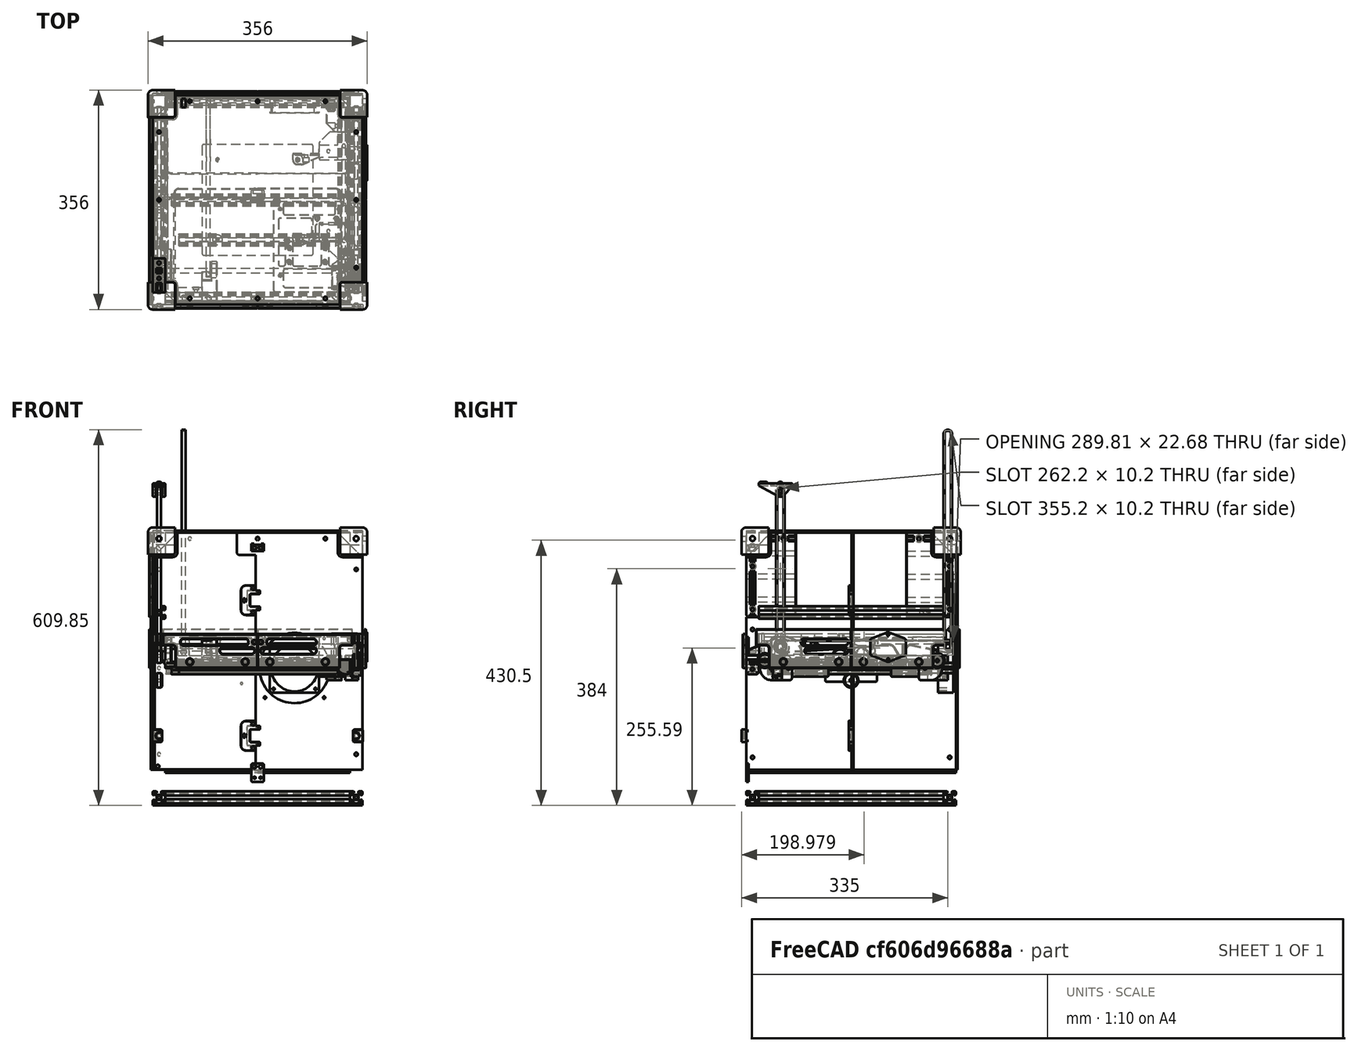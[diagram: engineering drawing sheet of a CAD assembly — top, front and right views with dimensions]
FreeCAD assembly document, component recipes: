
FREECAD ASSEMBLY — COMPONENT RECIPES ("assembly")

This assembly document has 26 components, labeled P0..P25 below (a component is one placed body or linked part). 25 of them carry a construction recipe — the FreeCAD feature program that regenerates the part from scratch, quoted from this document or its linked companion documents; the rest are supplied as boundary geometry only. No exploded tour is included for this assembly.
NOTE — document 2 of 3 of this assembly tour. The two overview renders and the header above are repeated from document 1; the component sections below continue where the previous document stopped.
COMPONENT P13 — recipe-attached ("electronics-mounting-plate", modeled in this document).
Construction recipe (the document's own serialized feature program — sketch geometry with constraints, then the solid features built on it; lengths are millimeters unless a unit is written):

FEATURE [Sketcher::SketchObject] Sketch485
  ArcFitTolerance = 1e-06
  AttachmentSupport = -> [XY_Plane316]
  FullyConstrained = true
  MakeInternals = false
  MapMode = 5
  expr: Constraints[10] = Spreadsheet.side_length / 2 - 20
  expr: Constraints[9] = -Spreadsheet.side_length / 2 + 20
  sketch-geometry (108):
    g0: LineSegment StartX=29 StartY=3 StartZ=0 EndX=147 EndY=3 EndZ=0
    g1: LineSegment StartX=150 StartY=-1e-16 StartZ=0 EndX=150 EndY=-76.5 EndZ=0
    g2: LineSegment StartX=147 StartY=-79.5 StartZ=0 EndX=140.5 EndY=-79.5 EndZ=0
    g3: LineSegment StartX=139.5 StartY=-80.5 StartZ=0 EndX=139.5 EndY=-128 EndZ=0
    g4: LineSegment StartX=138 StartY=-129.5 StartZ=0 EndX=137.5 EndY=-129.5 EndZ=0
    g5: LineSegment StartX=129.5 StartY=-137.5 StartZ=0 EndX=129.5 EndY=-150 EndZ=0
    g6: LineSegment StartX=129.5 StartY=-150 StartZ=0 EndX=29 EndY=-150 EndZ=0
    g7: LineSegment StartX=26 StartY=-147 StartZ=0 EndX=26 EndY=0 EndZ=0
    g8: ArcOfCircle CenterX=29 CenterY=1e-16 CenterZ=0 NormalX=0 NormalY=0 NormalZ=1 AngleXU=0 Radius=3 StartAngle=1.5708 EndAngle=3.14159
    g9: GeomPoint [constr] X=26 Y=3 Z=0
    g10: ArcOfCircle CenterX=147 CenterY=-1e-16 CenterZ=0 NormalX=0 NormalY=0 NormalZ=1 AngleXU=0 Radius=3 StartAngle=0 EndAngle=1.5708
    g11: GeomPoint [constr] X=150 Y=3 Z=0
    g12: ArcOfCircle CenterX=29 CenterY=-147 CenterZ=0 NormalX=0 NormalY=0 NormalZ=1 AngleXU=0 Radius=3 StartAngle=3.14159 EndAngle=4.71239
    g13: GeomPoint [constr] X=26 Y=-150 Z=0
    g14: ArcOfCircle CenterX=137.5 CenterY=-137.5 CenterZ=0 NormalX=0 NormalY=0 NormalZ=1 AngleXU=0 Radius=8 StartAngle=1.5708 EndAngle=3.14159
    g15: GeomPoint [constr] X=129.5 Y=-129.5 Z=0
    g16: ArcOfCircle CenterX=138 CenterY=-128 CenterZ=0 NormalX=0 NormalY=0 NormalZ=1 AngleXU=0 Radius=1.5 StartAngle=4.71239 EndAngle=6.28319
    g17: GeomPoint [constr] X=139.5 Y=-129.5 Z=0
    g18: ArcOfCircle CenterX=147 CenterY=-76.5 CenterZ=0 NormalX=0 NormalY=0 NormalZ=1 AngleXU=0 Radius=3 StartAngle=4.71239 EndAngle=6.28319
    g19: GeomPoint [constr] X=150 Y=-79.5 Z=0
    g20: ArcOfCircle CenterX=140.5 CenterY=-80.5 CenterZ=0 NormalX=0 NormalY=0 NormalZ=1 AngleXU=0 Radius=1 StartAngle=1.5708 EndAngle=3.14159
    g21: GeomPoint [constr] X=139.5 Y=-79.5 Z=0
    g22: LineSegment StartX=42 StartY=-116 StartZ=0 EndX=42 EndY=-139 EndZ=0
    g23: LineSegment StartX=45 StartY=-142 StartZ=0 EndX=118.5 EndY=-142 EndZ=0
    g24: LineSegment StartX=121.5 StartY=-139 StartZ=0 EndX=121.5 EndY=-116 EndZ=0
    g25: LineSegment StartX=118.5 StartY=-113 StartZ=0 EndX=45 EndY=-113 EndZ=0
    g26: LineSegment StartX=34 StartY=-33 StartZ=0 EndX=34 EndY=-58 EndZ=0
    g27: LineSegment StartX=37 StartY=-61 StartZ=0 EndX=85 EndY=-61 EndZ=0
    g28: LineSegment StartX=88 StartY=-58 StartZ=0 EndX=88 EndY=-33 EndZ=0
    g29: LineSegment StartX=85 StartY=-30 StartZ=0 EndX=37 EndY=-30 EndZ=0
    g30: LineSegment StartX=42 StartY=-8 StartZ=0 EndX=42 EndY=-21 EndZ=0
    g31: LineSegment StartX=45 StartY=-24 StartZ=0 EndX=123 EndY=-24 EndZ=0
    g32: LineSegment StartX=126 StartY=-21 StartZ=0 EndX=126 EndY=-8 EndZ=0
    g33: LineSegment StartX=123 StartY=-5 StartZ=0 EndX=45 EndY=-5 EndZ=0
    g34: LineSegment StartX=57 StartY=-70 StartZ=0 EndX=57 EndY=-104 EndZ=0
    g35: LineSegment StartX=60 StartY=-107 StartZ=0 EndX=100.5 EndY=-107 EndZ=0
    g36: LineSegment StartX=103.5 StartY=-104 StartZ=0 EndX=103.5 EndY=-70 EndZ=0
    g37: LineSegment StartX=100.5 StartY=-67 StartZ=0 EndX=60 EndY=-67 EndZ=0
    g38: LineSegment StartX=34 StartY=-76 StartZ=0 EndX=34 EndY=-104 EndZ=0
    g39: LineSegment StartX=37 StartY=-107 StartZ=0 EndX=42 EndY=-107 EndZ=0
    g40: LineSegment StartX=45 StartY=-104 StartZ=0 EndX=45 EndY=-76 EndZ=0
    g41: LineSegment StartX=42 StartY=-73 StartZ=0 EndX=37 EndY=-73 EndZ=0
    g42: LineSegment StartX=115.5 StartY=-70 StartZ=0 EndX=115.5 EndY=-104 EndZ=0
    g43: LineSegment StartX=118.5 StartY=-107 StartZ=0 EndX=128.5 EndY=-107 EndZ=0
    g44: LineSegment StartX=131.5 StartY=-104 StartZ=0 EndX=131.5 EndY=-70 EndZ=0
    g45: LineSegment StartX=128.5 StartY=-67 StartZ=0 EndX=118.5 EndY=-67 EndZ=0
    g46: LineSegment StartX=94 StartY=-43 StartZ=0 EndX=94 EndY=-58 EndZ=0
    g47: LineSegment StartX=97 StartY=-61 StartZ=0 EndX=139 EndY=-61 EndZ=0
    g48: LineSegment StartX=142 StartY=-58 StartZ=0 EndX=142 EndY=-43 EndZ=0
    g49: LineSegment StartX=139 StartY=-40 StartZ=0 EndX=97 EndY=-40 EndZ=0
    g50: GeomPoint X=109.5 Y=-67 Z=0
    g51: GeomPoint X=51 Y=-107 Z=0
    g52: ArcOfCircle CenterX=45 CenterY=-8 CenterZ=0 NormalX=0 NormalY=0 NormalZ=1 AngleXU=0 Radius=3 StartAngle=1.5708 EndAngle=3.14159
    g53: GeomPoint [constr] X=42 Y=-5 Z=0
    g54: ArcOfCircle CenterX=45 CenterY=-21 CenterZ=0 NormalX=0 NormalY=0 NormalZ=1 AngleXU=0 Radius=3 StartAngle=3.14159 EndAngle=4.71239
    g55: GeomPoint [constr] X=42 Y=-24 Z=0
    g56: ArcOfCircle CenterX=123 CenterY=-21 CenterZ=0 NormalX=0 NormalY=0 NormalZ=1 AngleXU=0 Radius=3 StartAngle=4.71239 EndAngle=6.28319
    g57: GeomPoint [constr] X=126 Y=-24 Z=0
    g58: ArcOfCircle CenterX=123 CenterY=-8 CenterZ=0 NormalX=0 NormalY=0 NormalZ=1 AngleXU=0 Radius=3 StartAngle=0 EndAngle=1.5708
    g59: GeomPoint [constr] X=126 Y=-5 Z=0
    g60: ArcOfCircle CenterX=37 CenterY=-33 CenterZ=0 NormalX=0 NormalY=0 NormalZ=1 AngleXU=0 Radius=3 StartAngle=1.5708 EndAngle=3.14159
    g61: GeomPoint [constr] X=34 Y=-30 Z=0
    g62: ArcOfCircle CenterX=85 CenterY=-33 CenterZ=0 NormalX=0 NormalY=0 NormalZ=1 AngleXU=0 Radius=3 StartAngle=2e-16 EndAngle=1.5708
    g63: GeomPoint [constr] X=88 Y=-30 Z=0
    g64: ArcOfCircle CenterX=85 CenterY=-58 CenterZ=0 NormalX=0 NormalY=0 NormalZ=1 AngleXU=0 Radius=3 StartAngle=4.71239 EndAngle=6.28319
    g65: GeomPoint [constr] X=88 Y=-61 Z=0
    g66: ArcOfCircle CenterX=37 CenterY=-58 CenterZ=0 NormalX=0 NormalY=0 NormalZ=1 AngleXU=0 Radius=3 StartAngle=3.14159 EndAngle=4.71239
    g67: GeomPoint [constr] X=34 Y=-61 Z=0
    g68: ArcOfCircle CenterX=97 CenterY=-58 CenterZ=0 NormalX=0 NormalY=0 NormalZ=1 AngleXU=0 Radius=3 StartAngle=3.14159 EndAngle=4.71239
    g69: GeomPoint [constr] X=94 Y=-61 Z=0
    g70: ArcOfCircle CenterX=97 CenterY=-43 CenterZ=0 NormalX=0 NormalY=0 NormalZ=1 AngleXU=0 Radius=3 StartAngle=1.5708 EndAngle=3.14159
    g71: GeomPoint [constr] X=94 Y=-40 Z=0
    g72: ArcOfCircle CenterX=139 CenterY=-43 CenterZ=0 NormalX=0 NormalY=0 NormalZ=1 AngleXU=0 Radius=3 StartAngle=0 EndAngle=1.5708
    g73: GeomPoint [constr] X=142 Y=-40 Z=0
    g74: ArcOfCircle CenterX=139 CenterY=-58 CenterZ=0 NormalX=0 NormalY=0 NormalZ=1 AngleXU=0 Radius=3 StartAngle=4.71239 EndAngle=6.28319
    g75: GeomPoint [constr] X=142 Y=-61 Z=0
    g76: ArcOfCircle CenterX=42 CenterY=-104 CenterZ=0 NormalX=0 NormalY=0 NormalZ=1 AngleXU=0 Radius=3 StartAngle=4.71239 EndAngle=6.28319
    g77: GeomPoint [constr] X=45 Y=-107 Z=0
    g78: ArcOfCircle CenterX=37 CenterY=-104 CenterZ=0 NormalX=0 NormalY=0 NormalZ=1 AngleXU=0 Radius=3 StartAngle=3.14159 EndAngle=4.71239
    g79: GeomPoint [constr] X=34 Y=-107 Z=0
    g80: ArcOfCircle CenterX=37 CenterY=-76 CenterZ=0 NormalX=0 NormalY=0 NormalZ=1 AngleXU=0 Radius=3 StartAngle=1.5708 EndAngle=3.14159
    g81: GeomPoint [constr] X=34 Y=-73 Z=0
    g82: ArcOfCircle CenterX=42 CenterY=-76 CenterZ=0 NormalX=0 NormalY=0 NormalZ=1 AngleXU=0 Radius=3 StartAngle=1.6e-15 EndAngle=1.5708
    g83: GeomPoint [constr] X=45 Y=-73 Z=0
    g84: ArcOfCircle CenterX=60 CenterY=-70 CenterZ=0 NormalX=0 NormalY=0 NormalZ=1 AngleXU=0 Radius=3 StartAngle=1.5708 EndAngle=3.14159
    g85: GeomPoint [constr] X=57 Y=-67 Z=0
    g86: ArcOfCircle CenterX=100.5 CenterY=-70 CenterZ=0 NormalX=0 NormalY=0 NormalZ=1 AngleXU=0 Radius=3 StartAngle=1.6e-15 EndAngle=1.5708
    g87: GeomPoint [constr] X=103.5 Y=-67 Z=0
    g88: ArcOfCircle CenterX=100.5 CenterY=-104 CenterZ=0 NormalX=0 NormalY=0 NormalZ=1 AngleXU=0 Radius=3 StartAngle=4.71239 EndAngle=6.28319
    g89: GeomPoint [constr] X=103.5 Y=-107 Z=0
    g90: ArcOfCircle CenterX=60 CenterY=-104 CenterZ=0 NormalX=0 NormalY=0 NormalZ=1 AngleXU=0 Radius=3 StartAngle=3.14159 EndAngle=4.71239
    g91: GeomPoint [constr] X=57 Y=-107 Z=0
    g92: ArcOfCircle CenterX=118.5 CenterY=-70 CenterZ=0 NormalX=0 NormalY=0 NormalZ=1 AngleXU=0 Radius=3 StartAngle=1.5708 EndAngle=3.14159
    g93: GeomPoint [constr] X=115.5 Y=-67 Z=0
    g94: ArcOfCircle CenterX=128.5 CenterY=-70 CenterZ=0 NormalX=0 NormalY=0 NormalZ=1 AngleXU=0 Radius=3 StartAngle=4e-16 EndAngle=1.5708
    g95: GeomPoint [constr] X=131.5 Y=-67 Z=0
    g96: ArcOfCircle CenterX=128.5 CenterY=-104 CenterZ=0 NormalX=0 NormalY=0 NormalZ=1 AngleXU=0 Radius=3 StartAngle=4.71239 EndAngle=6.28319
    g97: GeomPoint [constr] X=131.5 Y=-107 Z=0
    g98: ArcOfCircle CenterX=118.5 CenterY=-104 CenterZ=0 NormalX=0 NormalY=0 NormalZ=1 AngleXU=0 Radius=3 StartAngle=3.14159 EndAngle=4.71239
    g99: GeomPoint [constr] X=115.5 Y=-107 Z=0
    g100: ArcOfCircle CenterX=45 CenterY=-116 CenterZ=0 NormalX=0 NormalY=0 NormalZ=1 AngleXU=0 Radius=3 StartAngle=1.5708 EndAngle=3.14159
    g101: GeomPoint [constr] X=42 Y=-113 Z=0
    g102: ArcOfCircle CenterX=45 CenterY=-139 CenterZ=0 NormalX=0 NormalY=0 NormalZ=1 AngleXU=0 Radius=3 StartAngle=3.14159 EndAngle=4.71239
    g103: GeomPoint [constr] X=42 Y=-142 Z=0
    g104: ArcOfCircle CenterX=118.5 CenterY=-139 CenterZ=0 NormalX=0 NormalY=0 NormalZ=1 AngleXU=0 Radius=3 StartAngle=4.71239 EndAngle=6.28319
    g105: GeomPoint [constr] X=121.5 Y=-142 Z=0
    g106: ArcOfCircle CenterX=118.5 CenterY=-116 CenterZ=0 NormalX=0 NormalY=0 NormalZ=1 AngleXU=0 Radius=3 StartAngle=1.7e-15 EndAngle=1.5708
    g107: GeomPoint [constr] X=121.5 Y=-113 Z=0
  constraints (250):
    c: Horizontal(g0)
    c: Vertical(g1)
    c: Horizontal(g2)
    c: Vertical(g3)
    c: Horizontal(g4)
    c: Vertical(g5)
    c: Coincident(g5,g6)
    c: Horizontal(g6)
    c: Vertical(g7)
    c: DistanceY(g13) = -150
    c: DistanceX(g11) = 150
    c: DistanceX(g9) = 26
    c: DistanceY(g9) = 3
    c: PointOnObject(g9,g0)
    c: PointOnObject(g9,g7)
    c: Tangent(g0,g8) = 1.5708
    c: Tangent(g7,g8) = 1.5708
    c: Radius(g8) = 3
    c: PointOnObject(g11,g0)
    c: PointOnObject(g11,g1)
    c: Tangent(g0,g10) = 1.5708
    c: Tangent(g1,g10) = 1.5708
    c: PointOnObject(g13,g6)
    c: PointOnObject(g13,g7)
    c: Tangent(g6,g12) = 1.5708
    c: Tangent(g7,g12) = 1.5708
    c: Equal(g12,g10)
    c: Equal(g10,g8)
    c: DistanceX(g21,g19) = 10.5
    c: DistanceY(g5,g19) = 70.5
    c: PointOnObject(g15,g4)
    c: PointOnObject(g15,g5)
    c: Tangent(g4,g14) = -1.5708
    c: Tangent(g5,g14) = -1.5708
    c: Radius(g14) = 8
    c: DistanceX(g5,g19) = 20.5
    c: DistanceY(g5,g17) = 20.5
    c: PointOnObject(g17,g3)
    c: PointOnObject(g17,g4)
    c: Tangent(g3,g16) = 1.5708
    c: Tangent(g4,g16) = 1.5708
    c: PointOnObject(g19,g2)
    c: Tangent(g1,g18) = 1.5708
    c: Tangent(g2,g18) = 1.5708
    c: Equal(g18,g10)
    c: Radius(g16) = 1.5
    c: PointOnObject(g19,g1)
    c: PointOnObject(g21,g2)
    c: PointOnObject(g21,g3)
    c: Tangent(g2,g20) = -1.5708
    c: Tangent(g3,g20) = -1.5708
    c: Radius(g20) = 1
    c: Vertical(g22)
    c: Vertical(g24)
    c: Horizontal(g23)
    c: Horizontal(g25)
    c: Vertical(g26)
    c: Vertical(g28)
    c: Horizontal(g27)
    c: Horizontal(g29)
    c: Vertical(g30)
    c: Vertical(g32)
    c: Horizontal(g31)
    c: Horizontal(g33)
    c: Vertical(g34)
    c: Vertical(g36)
    c: Horizontal(g35)
    c: Horizontal(g37)
    c: Vertical(g38)
    c: Vertical(g40)
    c: Horizontal(g39)
    c: Horizontal(g41)
    c: Vertical(g42)
    c: Vertical(g44)
    c: Horizontal(g43)
    c: Horizontal(g45)
    c: Vertical(g46)
    c: Vertical(g48)
    c: Horizontal(g47)
    c: Horizontal(g49)
    c: Horizontal(g65,g69)
    c: DistanceY(g53,g0) = 8
    c: DistanceY(g61,g55) = 6
    c: DistanceX(g65,g69) = 6
    c: DistanceY(g87,g69) = 6
    c: Horizontal(g93,g87)
    c: Horizontal(g91,g77)
    c: DistanceY(g101,g91) = 6
    c: DistanceX(g87,g93) = 12
    c: DistanceX(g77,g91) = 12
    c: Horizontal(g89,g99)
    c: DistanceX(g105,g5) = 8
    c: DistanceY(g6,g103) = 8
    c: DistanceX(g13,g103) = 16
    c: DistanceY(g83,g67) = 12
    c: DistanceX(g9,g53) = 16
    c: DistanceX(g9,g61) = 8
    c: Vertical(g81,g67)
    c: DistanceX(g59,g11) = 24
    c: DistanceY(g71,g57) = 16
    c: DistanceX(g97,g17) = 8
    c: Symmetric(g93,g87,g50)
    c: DistanceX(g50) = 109.5
    c: DistanceY(g67) = -61
    c: Symmetric(g91,g77,g51)
    c: DistanceX(g51) = 51
    c: DistanceX(g73,g19) = 8
    c: DistanceY(g63) = -30
    c: DistanceY(g77) = -107
    c: DistanceX(g63) = 88
    c: PointOnObject(g53,g30)
    c: PointOnObject(g53,g33)
    c: Tangent(g30,g52) = -1.5708
    c: Tangent(g33,g52) = -1.5708
    c: PointOnObject(g55,g30)
    c: PointOnObject(g55,g31)
    c: Tangent(g30,g54) = -1.5708
    c: Tangent(g31,g54) = -1.5708
    c: PointOnObject(g57,g31)
    c: PointOnObject(g57,g32)
    c: Tangent(g31,g56) = -1.5708
    c: Tangent(g32,g56) = -1.5708
    c: PointOnObject(g59,g32)
    c: PointOnObject(g59,g33)
    c: Tangent(g32,g58) = -1.5708
    c: Tangent(g33,g58) = -1.5708
    c: Equal(g52,g54)
    c: Equal(g54,g56)
    c: Equal(g56,g58)
    c: Radius(g58) = 3
    c: PointOnObject(g61,g26)
    c: PointOnObject(g61,g29)
    c: Tangent(g26,g60) = -1.5708
    c: Tangent(g29,g60) = -1.5708
    c: PointOnObject(g63,g28)
    c: PointOnObject(g63,g29)
    c: Tangent(g28,g62) = -1.5708
    c: Tangent(g29,g62) = -1.5708
    c: PointOnObject(g65,g27)
    c: PointOnObject(g65,g28)
    c: Tangent(g27,g64) = -1.5708
    c: Tangent(g28,g64) = -1.5708
    c: PointOnObject(g67,g26)
    c: PointOnObject(g67,g27)
    c: Tangent(g26,g66) = -1.5708
    c: Tangent(g27,g66) = -1.5708
    c: Equal(g66,g60)
    c: Equal(g60,g62)
    c: Equal(g62,g64)
    c: Equal(g64,g54)
    c: PointOnObject(g69,g46)
    c: PointOnObject(g69,g47)
    c: Tangent(g46,g68) = -1.5708
    c: Tangent(g47,g68) = -1.5708
    c: PointOnObject(g71,g46)
    c: PointOnObject(g71,g49)
    c: Tangent(g46,g70) = -1.5708
    c: Tangent(g49,g70) = -1.5708
    c: PointOnObject(g73,g48)
    c: PointOnObject(g73,g49)
    c: Tangent(g48,g72) = -1.5708
    c: Tangent(g49,g72) = -1.5708
    c: PointOnObject(g75,g47)
    c: PointOnObject(g75,g48)
    c: Tangent(g47,g74) = -1.5708
    c: Tangent(g48,g74) = -1.5708
    c: Equal(g74,g72)
    c: Equal(g72,g70)
    c: Equal(g70,g68)
    c: Equal(g68,g64)
    c: PointOnObject(g77,g39)
    c: PointOnObject(g77,g40)
    c: Tangent(g39,g76) = -1.5708
    c: Tangent(g40,g76) = -1.5708
    c: PointOnObject(g79,g38)
    c: PointOnObject(g79,g39)
    c: Tangent(g38,g78) = -1.5708
    c: Tangent(g39,g78) = -1.5708
    c: PointOnObject(g81,g38)
    c: PointOnObject(g81,g41)
    c: Tangent(g38,g80) = -1.5708
    c: Tangent(g41,g80) = -1.5708
    c: PointOnObject(g83,g40)
    c: PointOnObject(g83,g41)
    c: Tangent(g40,g82) = -1.5708
    c: Tangent(g41,g82) = -1.5708
    c: Equal(g80,g82)
    c: Equal(g82,g76)
    c: Equal(g76,g78)
    c: Equal(g78,g66)
    c: PointOnObject(g85,g34)
    c: PointOnObject(g85,g37)
    c: Tangent(g34,g84) = -1.5708
    c: Tangent(g37,g84) = -1.5708
    c: PointOnObject(g87,g36)
    c: PointOnObject(g87,g37)
    c: Tangent(g36,g86) = -1.5708
    c: Tangent(g37,g86) = -1.5708
    c: PointOnObject(g89,g35)
    c: PointOnObject(g89,g36)
    c: Tangent(g35,g88) = -1.5708
    c: Tangent(g36,g88) = -1.5708
    c: PointOnObject(g91,g34)
    c: PointOnObject(g91,g35)
    c: Tangent(g34,g90) = -1.5708
    c: Tangent(g35,g90) = -1.5708
    c: Equal(g90,g84)
    c: Equal(g84,g86)
    c: Equal(g86,g88)
    c: Equal(g88,g82)
    c: PointOnObject(g93,g42)
    c: PointOnObject(g93,g45)
    c: Tangent(g42,g92) = -1.5708
    c: Tangent(g45,g92) = -1.5708
    c: PointOnObject(g95,g44)
    c: PointOnObject(g95,g45)
    c: Tangent(g44,g94) = -1.5708
    c: Tangent(g45,g94) = -1.5708
    c: PointOnObject(g97,g43)
    c: PointOnObject(g97,g44)
    c: Tangent(g43,g96) = -1.5708
    c: Tangent(g44,g96) = -1.5708
    c: PointOnObject(g99,g42)
    c: PointOnObject(g99,g43)
    c: Tangent(g42,g98) = -1.5708
    c: Tangent(g43,g98) = -1.5708
    c: Equal(g98,g96)
    c: Equal(g96,g94)
    c: Equal(g94,g92)
    c: Equal(g92,g86)
    c: PointOnObject(g101,g22)
    c: PointOnObject(g101,g25)
    c: Tangent(g22,g100) = -1.5708
    c: Tangent(g25,g100) = -1.5708
    c: PointOnObject(g103,g22)
    c: PointOnObject(g103,g23)
    c: Tangent(g22,g102) = -1.5708
    c: Tangent(g23,g102) = -1.5708
    c: PointOnObject(g105,g23)
    c: PointOnObject(g105,g24)
    c: Tangent(g23,g104) = -1.5708
    c: Tangent(g24,g104) = -1.5708
    c: PointOnObject(g107,g24)
    c: PointOnObject(g107,g25)
    c: Tangent(g24,g106) = -1.5708
    c: Tangent(g25,g106) = -1.5708
    c: Equal(g106,g104)
    c: Equal(g104,g100)
    c: Equal(g100,g102)
    c: Equal(g100,g78)
FEATURE [PartDesign::Pad] Pad109
  Direction = (0,0,1)
  Length = 4
  Length2 = 10
  Profile = -> Sketch485
  ReferenceAxis = -> Sketch485 [N_Axis]
  Suppressed = false
  Type = 0
FEATURE [Sketcher::SketchObject] Sketch486
  ArcFitTolerance = 1e-06
  AttachmentOffset = pos=(0,0,4) rot=(0,0,1;0rad)
  AttachmentSupport = -> [XY_Plane316]
  FullyConstrained = true
  MakeInternals = false
  MapMode = 5
  Placement = pos=(0,0,4) rot=(0,0,1;0rad)
  sketch-geometry (10):
    g0: Circle CenterX=32 CenterY=-2.5 CenterZ=0 NormalX=0 NormalY=0 NormalZ=1 AngleXU=0 Radius=3
    g1: Circle CenterX=96 CenterY=-29.5 CenterZ=0 NormalX=0 NormalY=0 NormalZ=1 AngleXU=0 Radius=3
    g2: Circle CenterX=128 CenterY=-32 CenterZ=0 NormalX=0 NormalY=0 NormalZ=1 AngleXU=0 Radius=3
    g3: Circle CenterX=47.5 CenterY=-67 CenterZ=0 NormalX=0 NormalY=0 NormalZ=1 AngleXU=0 Radius=3
    g4: Circle CenterX=109.5 CenterY=-67 CenterZ=0 NormalX=0 NormalY=0 NormalZ=1 AngleXU=0 Radius=3
    g5: Circle CenterX=51 CenterY=-78.5 CenterZ=0 NormalX=0 NormalY=0 NormalZ=1 AngleXU=0 Radius=2.5
    g6: Circle CenterX=109 CenterY=-78.5 CenterZ=0 NormalX=0 NormalY=0 NormalZ=1 AngleXU=0 Radius=2.5
    g7: Circle CenterX=109 CenterY=-101.5 CenterZ=0 NormalX=0 NormalY=0 NormalZ=1 AngleXU=0 Radius=2.5
    g8: Circle CenterX=51 CenterY=-101.5 CenterZ=0 NormalX=0 NormalY=0 NormalZ=1 AngleXU=0 Radius=2.5
    g9: GeomPoint X=80 Y=-90 Z=0
  constraints (28):
    c: Equal(g0,g3)
    c: Equal(g3,g1)
    c: Equal(g1,g4)
    c: Equal(g4,g2)
    c: Diameter(g0) = 6
    c: DistanceX(g0) = 32
    c: DistanceY(g0) = -2.5
    c: Horizontal(g3,g4)
    c: DistanceY(g3) = -67
    c: DistanceX(g3) = 47.5
    c: DistanceX(g4) = 109.5
    c: DistanceX(g1) = 96
    c: DistanceY(g2,g1) = 2.5
    c: DistanceY(g1) = -29.5
    c: DistanceX(g2) = 128
    c: Equal(g5,g6)
    c: Equal(g6,g7)
    c: Equal(g7,g8)
    c: Diameter(g8) = 5
    c: Vertical(g8,g5)
    c: Vertical(g6,g7)
    c: Horizontal(g6,g5)
    c: Horizontal(g8,g7)
    c: Symmetric(g6,g8,g9)
    c: DistanceX(g9) = 80
    c: DistanceY(g9) = -90
    c: DistanceY(g8,g5) = 23
    c: DistanceX(g5,g6) = 58
FEATURE [PartDesign::Pad] Pad110
  BaseFeature = -> Pad109
  Direction = (0,0,1)
  Length = 3
  Length2 = 10
  Profile = -> Sketch486
  ReferenceAxis = -> Sketch486 [N_Axis]
  Suppressed = false
  Type = 0
FEATURE [Sketcher::SketchObject] Sketch487
  ArcFitTolerance = 1e-06
  AttachmentOffset = pos=(0,0,4.3) rot=(0,0,1;0rad)
  AttachmentSupport = -> [XY_Plane316]
  FullyConstrained = true
  MakeInternals = false
  MapMode = 5
  Placement = pos=(0,0,4.3) rot=(0,0,1;0rad)
  sketch-geometry (10):
    g0: Circle CenterX=32 CenterY=-2.5 CenterZ=0 NormalX=0 NormalY=0 NormalZ=1 AngleXU=0 Radius=1.75
    g1: Circle CenterX=96 CenterY=-29.5 CenterZ=0 NormalX=0 NormalY=0 NormalZ=1 AngleXU=0 Radius=1.75
    g2: Circle CenterX=128 CenterY=-32 CenterZ=0 NormalX=0 NormalY=0 NormalZ=1 AngleXU=0 Radius=1.75
    g3: Circle CenterX=47.5 CenterY=-67 CenterZ=0 NormalX=0 NormalY=0 NormalZ=1 AngleXU=0 Radius=1.75
    g4: Circle CenterX=109.5 CenterY=-67 CenterZ=0 NormalX=0 NormalY=0 NormalZ=1 AngleXU=0 Radius=1.75
    g5: Circle CenterX=51 CenterY=-78.5 CenterZ=0 NormalX=0 NormalY=0 NormalZ=1 AngleXU=0 Radius=1.5
    g6: Circle CenterX=109 CenterY=-78.5 CenterZ=0 NormalX=0 NormalY=0 NormalZ=1 AngleXU=0 Radius=1.5
    g7: Circle CenterX=109 CenterY=-101.5 CenterZ=0 NormalX=0 NormalY=0 NormalZ=1 AngleXU=0 Radius=1.5
    g8: Circle CenterX=51 CenterY=-101.5 CenterZ=0 NormalX=0 NormalY=0 NormalZ=1 AngleXU=0 Radius=1.5
    g9: GeomPoint X=80 Y=-90 Z=0
  constraints (28):
    c: Equal(g0,g3)
    c: Equal(g3,g1)
    c: Equal(g1,g4)
    c: Equal(g4,g2)
    c: Diameter(g0) = 3.5
    c: DistanceX(g0) = 32
    c: DistanceY(g0) = -2.5
    c: Horizontal(g3,g4)
    c: DistanceY(g3) = -67
    c: DistanceX(g3) = 47.5
    c: DistanceX(g4) = 109.5
    c: DistanceX(g1) = 96
    c: DistanceY(g2,g1) = 2.5
    c: DistanceY(g1) = -29.5
    c: DistanceX(g2) = 128
    c: Equal(g5,g6)
    c: Equal(g6,g7)
    c: Equal(g7,g8)
    c: Diameter(g8) = 3
    c: Vertical(g8,g5)
    c: Vertical(g6,g7)
    c: Horizontal(g6,g5)
    c: Horizontal(g8,g7)
    c: Symmetric(g6,g8,g9)
    c: DistanceX(g9) = 80
    c: DistanceY(g9) = -90
    c: DistanceY(g8,g5) = 23
    c: DistanceX(g5,g6) = 58
FEATURE [Sketcher::SketchObject] Sketch488
  ArcFitTolerance = 1e-06
  AttachmentOffset = pos=(0,0,4) rot=(0,0,1;0rad)
  AttachmentSupport = -> [XY_Plane316]
  FullyConstrained = true
  MakeInternals = false
  MapMode = 5
  Placement = pos=(0,0,4) rot=(0,0,1;0rad)
  sketch-geometry (73):
    g0: Circle [constr] CenterX=32 CenterY=-2.5 CenterZ=0 NormalX=0 NormalY=0 NormalZ=1 AngleXU=0 Radius=3.17543
    g1: Circle [constr] CenterX=96 CenterY=-29.5 CenterZ=0 NormalX=0 NormalY=0 NormalZ=1 AngleXU=0 Radius=3.17543
    g2: Circle [constr] CenterX=128 CenterY=-32 CenterZ=0 NormalX=0 NormalY=0 NormalZ=1 AngleXU=0 Radius=3.17543
    g3: Circle [constr] CenterX=47.5 CenterY=-67 CenterZ=0 NormalX=0 NormalY=0 NormalZ=1 AngleXU=0 Radius=3.17543
    g4: Circle [constr] CenterX=109.5 CenterY=-67 CenterZ=0 NormalX=0 NormalY=0 NormalZ=1 AngleXU=0 Radius=3.17543
    g5: Circle [constr] CenterX=51 CenterY=-78.5 CenterZ=0 NormalX=0 NormalY=0 NormalZ=1 AngleXU=0 Radius=2.82902
    g6: Circle [constr] CenterX=109 CenterY=-78.5 CenterZ=0 NormalX=0 NormalY=0 NormalZ=1 AngleXU=0 Radius=2.82902
    g7: Circle [constr] CenterX=109 CenterY=-101.5 CenterZ=0 NormalX=0 NormalY=0 NormalZ=1 AngleXU=0 Radius=2.82902
    g8: Circle [constr] CenterX=51 CenterY=-101.5 CenterZ=0 NormalX=0 NormalY=0 NormalZ=1 AngleXU=0 Radius=2.82902
    g9: GeomPoint X=80 Y=-90 Z=0
    g10: LineSegment StartX=35.1754 StartY=-2.5 StartZ=0 EndX=33.5877 EndY=0.25 EndZ=0
    g11: LineSegment StartX=33.5877 StartY=0.25 StartZ=0 EndX=30.4123 EndY=0.25 EndZ=0
    g12: LineSegment StartX=30.4123 StartY=0.25 StartZ=0 EndX=28.8246 EndY=-2.5 EndZ=0
    g13: LineSegment StartX=28.8246 StartY=-2.5 StartZ=0 EndX=30.4123 EndY=-5.25 EndZ=0
    g14: LineSegment StartX=30.4123 StartY=-5.25 StartZ=0 EndX=33.5877 EndY=-5.25 EndZ=0
    g15: LineSegment StartX=33.5877 StartY=-5.25 StartZ=0 EndX=35.1754 EndY=-2.5 EndZ=0
    g16: Circle [constr] CenterX=32 CenterY=-2.5 CenterZ=0 NormalX=0 NormalY=0 NormalZ=1 AngleXU=0 Radius=3.17543
    g17: LineSegment StartX=99.1754 StartY=-29.5 StartZ=0 EndX=97.5877 EndY=-26.75 EndZ=0
    g18: LineSegment StartX=97.5877 StartY=-26.75 StartZ=0 EndX=94.4123 EndY=-26.75 EndZ=0
    g19: LineSegment StartX=94.4123 StartY=-26.75 StartZ=0 EndX=92.8246 EndY=-29.5 EndZ=0
    g20: LineSegment StartX=92.8246 StartY=-29.5 StartZ=0 EndX=94.4123 EndY=-32.25 EndZ=0
    g21: LineSegment StartX=94.4123 StartY=-32.25 StartZ=0 EndX=97.5877 EndY=-32.25 EndZ=0
    g22: LineSegment StartX=97.5877 StartY=-32.25 StartZ=0 EndX=99.1754 EndY=-29.5 EndZ=0
    g23: Circle [constr] CenterX=96 CenterY=-29.5 CenterZ=0 NormalX=0 NormalY=0 NormalZ=1 AngleXU=0 Radius=3.17543
    g24: LineSegment StartX=131.175 StartY=-32 StartZ=0 EndX=129.588 EndY=-29.25 EndZ=0
    g25: LineSegment StartX=129.588 StartY=-29.25 StartZ=0 EndX=126.412 EndY=-29.25 EndZ=0
    g26: LineSegment StartX=126.412 StartY=-29.25 StartZ=0 EndX=124.825 EndY=-32 EndZ=0
    g27: LineSegment StartX=124.825 StartY=-32 StartZ=0 EndX=126.412 EndY=-34.75 EndZ=0
    g28: LineSegment StartX=126.412 StartY=-34.75 StartZ=0 EndX=129.588 EndY=-34.75 EndZ=0
    g29: LineSegment StartX=129.588 StartY=-34.75 StartZ=0 EndX=131.175 EndY=-32 EndZ=0
    g30: Circle [constr] CenterX=128 CenterY=-32 CenterZ=0 NormalX=0 NormalY=0 NormalZ=1 AngleXU=0 Radius=3.17543
    g31: LineSegment StartX=50.6754 StartY=-67 StartZ=0 EndX=49.0877 EndY=-64.25 EndZ=0
    g32: LineSegment StartX=49.0877 StartY=-64.25 StartZ=0 EndX=45.9123 EndY=-64.25 EndZ=0
    g33: LineSegment StartX=45.9123 StartY=-64.25 StartZ=0 EndX=44.3246 EndY=-67 EndZ=0
    g34: LineSegment StartX=44.3246 StartY=-67 StartZ=0 EndX=45.9123 EndY=-69.75 EndZ=0
    g35: LineSegment StartX=45.9123 StartY=-69.75 StartZ=0 EndX=49.0877 EndY=-69.75 EndZ=0
    g36: LineSegment StartX=49.0877 StartY=-69.75 StartZ=0 EndX=50.6754 EndY=-67 EndZ=0
    g37: Circle [constr] CenterX=47.5 CenterY=-67 CenterZ=0 NormalX=0 NormalY=0 NormalZ=1 AngleXU=0 Radius=3.17543
    g38: LineSegment StartX=112.675 StartY=-67 StartZ=0 EndX=111.088 EndY=-64.25 EndZ=0
    g39: LineSegment StartX=111.088 StartY=-64.25 StartZ=0 EndX=107.912 EndY=-64.25 EndZ=0
    g40: LineSegment StartX=107.912 StartY=-64.25 StartZ=0 EndX=106.325 EndY=-67 EndZ=0
    g41: LineSegment StartX=106.325 StartY=-67 StartZ=0 EndX=107.912 EndY=-69.75 EndZ=0
    g42: LineSegment StartX=107.912 StartY=-69.75 StartZ=0 EndX=111.088 EndY=-69.75 EndZ=0
    g43: LineSegment StartX=111.088 StartY=-69.75 StartZ=0 EndX=112.675 EndY=-67 EndZ=0
    g44: Circle [constr] CenterX=109.5 CenterY=-67 CenterZ=0 NormalX=0 NormalY=0 NormalZ=1 AngleXU=0 Radius=3.17543
    g45: LineSegment StartX=53.829 StartY=-78.5 StartZ=0 EndX=52.4145 EndY=-76.05 EndZ=0
    g46: LineSegment StartX=52.4145 StartY=-76.05 StartZ=0 EndX=49.5855 EndY=-76.05 EndZ=0
    g47: LineSegment StartX=49.5855 StartY=-76.05 StartZ=0 EndX=48.171 EndY=-78.5 EndZ=0
    g48: LineSegment StartX=48.171 StartY=-78.5 StartZ=0 EndX=49.5855 EndY=-80.95 EndZ=0
    g49: LineSegment StartX=49.5855 StartY=-80.95 StartZ=0 EndX=52.4145 EndY=-80.95 EndZ=0
    g50: LineSegment StartX=52.4145 StartY=-80.95 StartZ=0 EndX=53.829 EndY=-78.5 EndZ=0
    g51: Circle [constr] CenterX=51 CenterY=-78.5 CenterZ=0 NormalX=0 NormalY=0 NormalZ=1 AngleXU=0 Radius=2.82902
    g52: LineSegment StartX=111.829 StartY=-78.5 StartZ=0 EndX=110.415 EndY=-76.05 EndZ=0
    g53: LineSegment StartX=110.415 StartY=-76.05 StartZ=0 EndX=107.585 EndY=-76.05 EndZ=0
    g54: LineSegment StartX=107.585 StartY=-76.05 StartZ=0 EndX=106.171 EndY=-78.5 EndZ=0
    g55: LineSegment StartX=106.171 StartY=-78.5 StartZ=0 EndX=107.585 EndY=-80.95 EndZ=0
    g56: LineSegment StartX=107.585 StartY=-80.95 StartZ=0 EndX=110.415 EndY=-80.95 EndZ=0
    g57: LineSegment StartX=110.415 StartY=-80.95 StartZ=0 EndX=111.829 EndY=-78.5 EndZ=0
    g58: Circle [constr] CenterX=109 CenterY=-78.5 CenterZ=0 NormalX=0 NormalY=0 NormalZ=1 AngleXU=0 Radius=2.82902
    g59: LineSegment StartX=111.829 StartY=-101.5 StartZ=0 EndX=110.415 EndY=-99.05 EndZ=0
    g60: LineSegment StartX=110.415 StartY=-99.05 StartZ=0 EndX=107.585 EndY=-99.05 EndZ=0
    g61: LineSegment StartX=107.585 StartY=-99.05 StartZ=0 EndX=106.171 EndY=-101.5 EndZ=0
    g62: LineSegment StartX=106.171 StartY=-101.5 StartZ=0 EndX=107.585 EndY=-103.95 EndZ=0
    g63: LineSegment StartX=107.585 StartY=-103.95 StartZ=0 EndX=110.415 EndY=-103.95 EndZ=0
    g64: LineSegment StartX=110.415 StartY=-103.95 StartZ=0 EndX=111.829 EndY=-101.5 EndZ=0
    g65: Circle [constr] CenterX=109 CenterY=-101.5 CenterZ=0 NormalX=0 NormalY=0 NormalZ=1 AngleXU=0 Radius=2.82902
    g66: LineSegment StartX=53.829 StartY=-101.5 StartZ=0 EndX=52.4145 EndY=-99.05 EndZ=0
    g67: LineSegment StartX=52.4145 StartY=-99.05 StartZ=0 EndX=49.5855 EndY=-99.05 EndZ=0
    g68: LineSegment StartX=49.5855 StartY=-99.05 StartZ=0 EndX=48.171 EndY=-101.5 EndZ=0
    g69: LineSegment StartX=48.171 StartY=-101.5 StartZ=0 EndX=49.5855 EndY=-103.95 EndZ=0
    g70: LineSegment StartX=49.5855 StartY=-103.95 StartZ=0 EndX=52.4145 EndY=-103.95 EndZ=0
    g71: LineSegment StartX=52.4145 StartY=-103.95 StartZ=0 EndX=53.829 EndY=-101.5 EndZ=0
    g72: Circle [constr] CenterX=51 CenterY=-101.5 CenterZ=0 NormalX=0 NormalY=0 NormalZ=1 AngleXU=0 Radius=2.82902
  constraints (172):
    c: Equal(g0,g3)
    c: Equal(g3,g1)
    c: Equal(g1,g4)
    c: Equal(g4,g2)
    c: DistanceX(g0) = 32
    c: DistanceY(g0) = -2.5
    c: Horizontal(g3,g4)
    c: DistanceY(g3) = -67
    c: DistanceX(g3) = 47.5
    c: DistanceX(g4) = 109.5
    c: DistanceX(g1) = 96
    c: DistanceY(g2,g1) = 2.5
    c: DistanceY(g1) = -29.5
    c: DistanceX(g2) = 128
    c: Equal(g5,g6)
    c: Equal(g6,g7)
    c: Equal(g7,g8)
    c: Vertical(g8,g5)
    c: Vertical(g6,g7)
    c: Horizontal(g6,g5)
    c: Horizontal(g8,g7)
    c: Symmetric(g6,g8,g9)
    c: DistanceX(g9) = 80
    c: DistanceY(g9) = -90
    c: DistanceY(g8,g5) = 23
    c: DistanceX(g5,g6) = 58
    c: Coincident(g10,g11)
    c: Coincident(g11,g12)
    c: Coincident(g12,g13)
    c: Coincident(g13,g14)
    c: Coincident(g14,g15)
    c: Coincident(g15,g10)
    c: Equal(g10, g11-g15) x5
    c: PointOnObject(g10,g16)
    c: PointOnObject(g11,g16)
    c: PointOnObject(g12,g16)
    c: PointOnObject(g13,g16)
    c: PointOnObject(g14,g16)
    c: PointOnObject(g15,g16)
    c: Coincident(g16,g0)
    c: PointOnObject(g15,g0)
    c: Horizontal(g11)
    c: DistanceY(g14,g10) = 5.5
    c: Coincident(g17,g18)
    c: Coincident(g18,g19)
    c: Coincident(g19,g20)
    c: Coincident(g20,g21)
    c: Coincident(g21,g22)
    c: Coincident(g22,g17)
    c: Equal(g17, g18-g22) x5
    c: PointOnObject(g17,g23)
    c: PointOnObject(g18,g23)
    c: PointOnObject(g19,g23)
    c: PointOnObject(g20,g23)
    c: PointOnObject(g21,g23)
    c: PointOnObject(g22,g23)
    c: Coincident(g23,g1)
    c: PointOnObject(g22,g1)
    c: Horizontal(g18)
    c: Coincident(g24,g25)
    c: Coincident(g25,g26)
    c: Coincident(g26,g27)
    c: Coincident(g27,g28)
    c: Coincident(g28,g29)
    c: Coincident(g29,g24)
    c: Equal(g24, g25-g29) x5
    c: PointOnObject(g24,g30)
    c: PointOnObject(g25,g30)
    c: PointOnObject(g26,g30)
    c: PointOnObject(g27,g30)
    c: PointOnObject(g28,g30)
    c: PointOnObject(g29,g30)
    c: Coincident(g30,g2)
    c: PointOnObject(g29,g2)
    c: Horizontal(g25)
    c: Coincident(g31,g32)
    c: Coincident(g32,g33)
    c: Coincident(g33,g34)
    c: Coincident(g34,g35)
    c: Coincident(g35,g36)
    c: Coincident(g36,g31)
    c: Equal(g31, g32-g36) x5
    c: PointOnObject(g31,g37)
    c: PointOnObject(g32,g37)
    c: PointOnObject(g33,g37)
    c: PointOnObject(g34,g37)
    c: PointOnObject(g35,g37)
    c: PointOnObject(g36,g37)
    c: Coincident(g37,g3)
    c: PointOnObject(g36,g3)
    c: Horizontal(g32)
    c: Coincident(g38,g39)
    c: Coincident(g39,g40)
    c: Coincident(g40,g41)
    c: Coincident(g41,g42)
    c: Coincident(g42,g43)
    c: Coincident(g43,g38)
    c: Equal(g38, g39-g43) x5
    c: PointOnObject(g38,g44)
    c: PointOnObject(g39,g44)
    c: PointOnObject(g40,g44)
    c: PointOnObject(g41,g44)
    c: PointOnObject(g42,g44)
    c: PointOnObject(g43,g44)
    c: Coincident(g44,g4)
    c: PointOnObject(g43,g4)
    c: Horizontal(g39)
    c: Coincident(g45,g46)
    c: Coincident(g46,g47)
    c: Coincident(g47,g48)
    c: Coincident(g48,g49)
    c: Coincident(g49,g50)
    c: Coincident(g50,g45)
    c: Equal(g45, g46-g50) x5
    c: PointOnObject(g45,g51)
    c: PointOnObject(g46,g51)
    c: PointOnObject(g47,g51)
    c: PointOnObject(g48,g51)
    c: PointOnObject(g49,g51)
    c: PointOnObject(g50,g51)
    c: Coincident(g51,g5)
    c: PointOnObject(g50,g5)
    c: Horizontal(g46)
    c: Coincident(g52,g53)
    c: Coincident(g53,g54)
    c: Coincident(g54,g55)
    c: Coincident(g55,g56)
    c: Coincident(g56,g57)
    c: Coincident(g57,g52)
    c: Equal(g52, g53-g57) x5
    c: PointOnObject(g52,g58)
    c: PointOnObject(g53,g58)
    c: PointOnObject(g54,g58)
    c: PointOnObject(g55,g58)
    c: PointOnObject(g56,g58)
    c: PointOnObject(g57,g58)
    c: Coincident(g58,g6)
    c: PointOnObject(g57,g6)
    c: Coincident(g59,g60)
    c: Coincident(g60,g61)
    c: Coincident(g61,g62)
    c: Coincident(g62,g63)
    c: Coincident(g63,g64)
    c: Coincident(g64,g59)
    c: Equal(g59, g60-g64) x5
    c: PointOnObject(g59,g65)
    c: PointOnObject(g60,g65)
    c: PointOnObject(g61,g65)
    c: PointOnObject(g62,g65)
    c: PointOnObject(g63,g65)
    c: PointOnObject(g64,g65)
    c: Coincident(g65,g7)
    c: PointOnObject(g64,g7)
    c: Coincident(g66,g67)
    c: Coincident(g67,g68)
    c: Coincident(g68,g69)
    c: Coincident(g69,g70)
    c: Coincident(g70,g71)
    c: Coincident(g71,g66)
    c: Equal(g66, g67-g71) x5
    c: PointOnObject(g66,g72)
    c: PointOnObject(g67,g72)
    c: PointOnObject(g68,g72)
    c: PointOnObject(g69,g72)
    c: PointOnObject(g70,g72)
    c: PointOnObject(g71,g72)
    c: Coincident(g72,g8)
    c: PointOnObject(g71,g8)
    c: Horizontal(g67)
    c: Horizontal(g60)
    c: Horizontal(g53)
    c: DistanceY(g70,g66) = 4.9
FEATURE [PartDesign::Chamfer] Chamfer021
  Angle = 45
  Base = -> Pad110 [Edge136,Edge127,Edge145,Edge154,Edge155,Edge108,Edge107,Edge118,Edge117]
  BaseFeature = -> Pad110
  ChamferType = 0
  FlipDirection = false
  Size = 2
  Size2 = 1
  SupportTransform = false
  Suppressed = false
  UseAllEdges = false
FEATURE [PartDesign::Pocket] Pocket341
  BaseFeature = -> Chamfer021
  Direction = (0,0,-1)
  Length = 5
  Length2 = 5
  Profile = -> Sketch487
  ReferenceAxis = -> Sketch487 [N_Axis]
  Reversed = true
  Suppressed = false
  Type = 1
FEATURE [PartDesign::Pocket] Pocket342
  BaseFeature = -> Pocket341
  Direction = (0,0,-1)
  Length = 5
  Length2 = 5
  Profile = -> Sketch488
  ReferenceAxis = -> Sketch488 [N_Axis]
  Suppressed = false
  Type = 1
FEATURE [Sketcher::SketchObject] Sketch489
  ArcFitTolerance = 1e-06
  AttachmentOffset = pos=(0,0,0.7) rot=(0,0,1;0rad)
  AttachmentSupport = -> [XY_Plane316]
  FullyConstrained = true
  MakeInternals = false
  MapMode = 5
  Placement = pos=(0,0,0.7) rot=(0,0,1;0rad)
  sketch-geometry (4):
    g0: Circle CenterX=37 CenterY=-15 CenterZ=0 NormalX=0 NormalY=0 NormalZ=1 AngleXU=0 Radius=1.75
    g1: Circle CenterX=132 CenterY=-15 CenterZ=0 NormalX=0 NormalY=0 NormalZ=1 AngleXU=0 Radius=1.75
    g2: Circle CenterX=37 CenterY=-123 CenterZ=0 NormalX=0 NormalY=0 NormalZ=1 AngleXU=0 Radius=1.75
    g3: Circle CenterX=132 CenterY=-123 CenterZ=0 NormalX=0 NormalY=0 NormalZ=1 AngleXU=0 Radius=1.75
  constraints (12):
    c: Horizontal(g2,g3)
    c: Equal(g2,g3)
    c: Diameter(g2) = 3.5
    c: Equal(g0,g1)
    c: Equal(g1,g3)
    c: Horizontal(g0,g1)
    c: Vertical(g1,g3)
    c: Vertical(g0,g2)
    c: DistanceX(g0) = 37
    c: DistanceY(g0) = -15
    c: DistanceX(g1) = 132
    c: DistanceY(g2) = -123
FEATURE [PartDesign::Pocket] Pocket343
  BaseFeature = -> Pocket342
  Direction = (0,0,-1)
  Length = 5
  Length2 = 5
  Midplane = true
  Profile = -> Sketch489
  ReferenceAxis = -> Sketch489 [N_Axis]
  Suppressed = false
  Type = 1
FEATURE [Sketcher::SketchObject] Sketch490
  ArcFitTolerance = 1e-06
  AttachmentOffset = pos=(0,0,1) rot=(0,0,1;0rad)
  AttachmentSupport = -> [XY_Plane316]
  FullyConstrained = true
  MakeInternals = false
  MapMode = 5
  Placement = pos=(0,0,1) rot=(0,0,1;0rad)
  sketch-geometry (28):
    g0: LineSegment StartX=38.5877 StartY=-17.75 StartZ=0 EndX=40.1754 EndY=-15 EndZ=0
    g1: LineSegment StartX=40.1754 StartY=-15 StartZ=0 EndX=38.5877 EndY=-12.25 EndZ=0
    g2: LineSegment StartX=38.5877 StartY=-12.25 StartZ=0 EndX=35.4123 EndY=-12.25 EndZ=0
    g3: LineSegment StartX=35.4123 StartY=-12.25 StartZ=0 EndX=33.8246 EndY=-15 EndZ=0
    g4: LineSegment StartX=33.8246 StartY=-15 StartZ=0 EndX=35.4123 EndY=-17.75 EndZ=0
    g5: LineSegment StartX=35.4123 StartY=-17.75 StartZ=0 EndX=38.5877 EndY=-17.75 EndZ=0
    g6: Circle [constr] CenterX=37 CenterY=-15 CenterZ=0 NormalX=0 NormalY=0 NormalZ=1 AngleXU=0 Radius=3.17543
    g7: LineSegment StartX=133.588 StartY=-17.75 StartZ=0 EndX=135.175 EndY=-15 EndZ=0
    g8: LineSegment StartX=135.175 StartY=-15 StartZ=0 EndX=133.588 EndY=-12.25 EndZ=0
    g9: LineSegment StartX=133.588 StartY=-12.25 StartZ=0 EndX=130.412 EndY=-12.25 EndZ=0
    g10: LineSegment StartX=130.412 StartY=-12.25 StartZ=0 EndX=128.825 EndY=-15 EndZ=0
    g11: LineSegment StartX=128.825 StartY=-15 StartZ=0 EndX=130.412 EndY=-17.75 EndZ=0
    g12: LineSegment StartX=130.412 StartY=-17.75 StartZ=0 EndX=133.588 EndY=-17.75 EndZ=0
    g13: Circle [constr] CenterX=132 CenterY=-15 CenterZ=0 NormalX=0 NormalY=0 NormalZ=1 AngleXU=0 Radius=3.17543
    g14: LineSegment StartX=133.588 StartY=-125.75 StartZ=0 EndX=135.175 EndY=-123 EndZ=0
    g15: LineSegment StartX=135.175 StartY=-123 StartZ=0 EndX=133.588 EndY=-120.25 EndZ=0
    g16: LineSegment StartX=133.588 StartY=-120.25 StartZ=0 EndX=130.412 EndY=-120.25 EndZ=0
    g17: LineSegment StartX=130.412 StartY=-120.25 StartZ=0 EndX=128.825 EndY=-123 EndZ=0
    g18: LineSegment StartX=128.825 StartY=-123 StartZ=0 EndX=130.412 EndY=-125.75 EndZ=0
    g19: LineSegment StartX=130.412 StartY=-125.75 StartZ=0 EndX=133.588 EndY=-125.75 EndZ=0
    g20: Circle [constr] CenterX=132 CenterY=-123 CenterZ=0 NormalX=0 NormalY=0 NormalZ=1 AngleXU=0 Radius=3.17543
    g21: LineSegment StartX=40.1754 StartY=-123 StartZ=0 EndX=38.5877 EndY=-120.25 EndZ=0
    g22: LineSegment StartX=38.5877 StartY=-120.25 StartZ=0 EndX=35.4123 EndY=-120.25 EndZ=0
    g23: LineSegment StartX=35.4123 StartY=-120.25 StartZ=0 EndX=33.8246 EndY=-123 EndZ=0
    g24: LineSegment StartX=33.8246 StartY=-123 StartZ=0 EndX=35.4123 EndY=-125.75 EndZ=0
    g25: LineSegment StartX=35.4123 StartY=-125.75 StartZ=0 EndX=38.5877 EndY=-125.75 EndZ=0
    g26: LineSegment StartX=38.5877 StartY=-125.75 StartZ=0 EndX=40.1754 EndY=-123 EndZ=0
    g27: Circle [constr] CenterX=37 CenterY=-123 CenterZ=0 NormalX=0 NormalY=0 NormalZ=1 AngleXU=0 Radius=3.17543
  constraints (68):
    c: Coincident(g0,g1)
    c: Coincident(g1,g2)
    c: Coincident(g2,g3)
    c: Coincident(g3,g4)
    c: Coincident(g4,g5)
    c: Coincident(g5,g0)
    c: Equal(g0, g1-g5) x5
    c: PointOnObject(g0,g6)
    c: PointOnObject(g1,g6)
    c: PointOnObject(g2,g6)
    c: PointOnObject(g3,g6)
    c: PointOnObject(g4,g6)
    c: PointOnObject(g5,g6)
    c: Coincident(g7,g8)
    c: Coincident(g8,g9)
    c: Coincident(g9,g10)
    c: Coincident(g10,g11)
    c: Coincident(g11,g12)
    c: Coincident(g12,g7)
    c: Equal(g7, g8-g12) x5
    c: PointOnObject(g7,g13)
    c: PointOnObject(g8,g13)
    c: PointOnObject(g9,g13)
    c: PointOnObject(g10,g13)
    c: PointOnObject(g11,g13)
    c: PointOnObject(g12,g13)
    c: Coincident(g14,g15)
    c: Coincident(g15,g16)
    c: Coincident(g16,g17)
    c: Coincident(g17,g18)
    c: Coincident(g18,g19)
    c: Coincident(g19,g14)
    c: Equal(g14, g15-g19) x5
    c: PointOnObject(g14,g20)
    c: PointOnObject(g15,g20)
    c: PointOnObject(g16,g20)
    c: PointOnObject(g17,g20)
    c: PointOnObject(g18,g20)
    c: PointOnObject(g19,g20)
    c: Coincident(g21,g22)
    c: Coincident(g22,g23)
    c: Coincident(g23,g24)
    c: Coincident(g24,g25)
    c: Coincident(g25,g26)
    c: Coincident(g26,g21)
    c: Equal(g21, g22-g26) x5
    c: PointOnObject(g21,g27)
    c: PointOnObject(g22,g27)
    c: PointOnObject(g23,g27)
    c: PointOnObject(g24,g27)
    c: PointOnObject(g25,g27)
    c: PointOnObject(g26,g27)
    c: Horizontal(g9)
    c: Horizontal(g16)
    c: Horizontal(g22)
    c: Horizontal(g2)
    c: Horizontal(g6,g13)
    c: Equal(g13,g6)
    c: Vertical(g6,g27)
    c: Equal(g27,g6)
    c: Horizontal(g27,g20)
    c: Equal(g20,g27)
    c: Vertical(g20,g13)
    c: DistanceY(g0,g1) = 5.5
    c: DistanceX(g6) = 37
    c: DistanceY(g6) = -15
    c: DistanceX(g13) = 132
    c: DistanceY(g27) = -123
FEATURE [PartDesign::Pocket] Pocket344
  BaseFeature = -> Pocket343
  Direction = (0,0,-1)
  Length = 5
  Length2 = 5
  Profile = -> Sketch490
  ReferenceAxis = -> Sketch490 [N_Axis]
  Reversed = true
  Suppressed = false
  Type = 1
FEATURE [PartDesign::Chamfer] Chamfer022
  Angle = 45
  Base = -> Pocket344 [Face106]
  BaseFeature = -> Pocket344
  ChamferType = 0
  FlipDirection = false
  Size = 0.5
  Size2 = 1
  SupportTransform = false
  Suppressed = false
  UseAllEdges = false
FEATURE [PartDesign::Body] Body165  label="electronics-mounting-plate"
  AllowCompound = false
  Group = -> [Sketch485,Pad109,Sketch486,Pad110,Sketch487,Sketch488,Chamfer021,Pocket341,Pocket342,Sketch489,Pocket343,Sketch490,Pocket344,Chamfer022]
  Origin = -> Origin317
  Tip = -> Chamfer022
COMPONENT P14 — recipe-attached ("z-motion-back-idler-mount-right", modeled in this document).
Construction recipe (the document's own serialized feature program — sketch geometry with constraints, then the solid features built on it; lengths are millimeters unless a unit is written):

FEATURE [Sketcher::SketchObject] Sketch011  label="belt-sketch"
  ArcFitTolerance = 0
  AttachmentSupport = -> [XY_Plane021]
  FullyConstrained = true
  MakeInternals = false
  MapMode = 5
  expr: Constraints[5] = -(Spreadsheet.side_length / 2 - 20)
  expr: Constraints[6] = Spreadsheet.side_length / 2 - 20
  expr: Constraints[70] = Spreadsheet.x_position
  expr: Constraints[74] = Spreadsheet.y_position + 30
  sketch-geometry (36):
    g0: Circle [constr] CenterX=-141 CenterY=-128 CenterZ=0 NormalX=0 NormalY=0 NormalZ=1 AngleXU=0 Radius=6.1
    g1: Circle [constr] CenterX=-141 CenterY=49 CenterZ=0 NormalX=0 NormalY=0 NormalZ=1 AngleXU=0 Radius=6.1
    g2: Circle [constr] CenterX=-141 CenterY=160 CenterZ=0 NormalX=0 NormalY=0 NormalZ=1 AngleXU=0 Radius=6.1
    g3: Circle [constr] CenterX=141 CenterY=49 CenterZ=0 NormalX=0 NormalY=0 NormalZ=1 AngleXU=0 Radius=6.1
    g4: Circle [constr] CenterX=141 CenterY=160 CenterZ=0 NormalX=0 NormalY=0 NormalZ=1 AngleXU=0 Radius=6.1
    g5: GeomPoint [constr] X=-150 Y=150 Z=0
    g6: GeomPoint [constr] X=-150 Y=-150 Z=0
    g7: GeomPoint [constr] X=-150 Y=30 Z=0
    g8: GeomPoint [constr] X=-128.17 Y=49 Z=0
    g9: LineSegment StartX=-135.65 StartY=-128 StartZ=0 EndX=-135.65 EndY=11 EndZ=0
    g10: LineSegment StartX=-134.27 StartY=11 StartZ=0 EndX=-134.27 EndY=-128 EndZ=0
    g11: GeomPoint [constr] X=-134.9 Y=-128 Z=0
    g12: ArcOfCircle CenterX=-128.17 CenterY=11 CenterZ=0 NormalX=0 NormalY=0 NormalZ=1 AngleXU=0 Radius=6.1 StartAngle=1.5708 EndAngle=3.14159
    g13: ArcOfCircle CenterX=-128.17 CenterY=11 CenterZ=0 NormalX=0 NormalY=0 NormalZ=1 AngleXU=0 Radius=7.48 StartAngle=1.5708 EndAngle=3.14159
    g14: LineSegment StartX=-128.17 StartY=17.1 StartZ=0 EndX=0 EndY=17.1 EndZ=0
    g15: LineSegment StartX=-128.17 StartY=18.48 StartZ=0 EndX=0 EndY=18.48 EndZ=0
    g16: LineSegment StartX=0 StartY=18.48 StartZ=0 EndX=0 EndY=17.1 EndZ=0
    g17: ArcOfCircle CenterX=-141 CenterY=-128 CenterZ=0 NormalX=0 NormalY=0 NormalZ=1 AngleXU=0 Radius=5.35 StartAngle=3.14159 EndAngle=6.28319
    g18: ArcOfCircle CenterX=-141 CenterY=-128 CenterZ=0 NormalX=0 NormalY=0 NormalZ=1 AngleXU=0 Radius=6.73 StartAngle=3.14159 EndAngle=6.28319
    g19: LineSegment StartX=-146.35 StartY=-128 StartZ=0 EndX=-146.35 EndY=160 EndZ=0
    g20: LineSegment StartX=-147.73 StartY=160 StartZ=0 EndX=-147.73 EndY=-128 EndZ=0
    g21: ArcOfCircle CenterX=-141 CenterY=160 CenterZ=0 NormalX=0 NormalY=0 NormalZ=1 AngleXU=0 Radius=5.35 StartAngle=1.5708 EndAngle=3.14159
    g22: ArcOfCircle CenterX=-141 CenterY=160 CenterZ=0 NormalX=0 NormalY=0 NormalZ=1 AngleXU=0 Radius=6.73 StartAngle=1.5708 EndAngle=3.14159
    g23: LineSegment StartX=-141 StartY=165.35 StartZ=0 EndX=141 EndY=165.35 EndZ=0
    g24: LineSegment StartX=141 StartY=166.73 StartZ=0 EndX=-141 EndY=166.73 EndZ=0
    g25: ArcOfCircle CenterX=141 CenterY=160 CenterZ=0 NormalX=0 NormalY=0 NormalZ=1 AngleXU=0 Radius=5.35 StartAngle=-1.8e-15 EndAngle=1.5708
    g26: ArcOfCircle CenterX=141 CenterY=160 CenterZ=0 NormalX=0 NormalY=0 NormalZ=1 AngleXU=0 Radius=6.73 StartAngle=1.9e-15 EndAngle=1.5708
    g27: LineSegment StartX=146.35 StartY=160 StartZ=0 EndX=146.35 EndY=49 EndZ=0
    g28: LineSegment StartX=147.73 StartY=49 StartZ=0 EndX=147.73 EndY=160 EndZ=0
    g29: ArcOfCircle CenterX=141 CenterY=49 CenterZ=0 NormalX=0 NormalY=0 NormalZ=1 AngleXU=0 Radius=5.35 StartAngle=4.71239 EndAngle=6.28319
    g30: ArcOfCircle CenterX=141 CenterY=49 CenterZ=0 NormalX=0 NormalY=0 NormalZ=1 AngleXU=0 Radius=6.73 StartAngle=4.71239 EndAngle=6.28319
    g31: LineSegment StartX=141 StartY=42.27 StartZ=0 EndX=0 EndY=42.27 EndZ=0
    g32: LineSegment StartX=0 StartY=43.65 StartZ=0 EndX=141 EndY=43.65 EndZ=0
    g33: LineSegment StartX=0 StartY=43.65 StartZ=0 EndX=0 EndY=42.27 EndZ=0
    g34: GeomPoint [constr] X=-128.17 Y=30 Z=0
    g35: Circle [constr] CenterX=-128.17 CenterY=11 CenterZ=0 NormalX=0 NormalY=0 NormalZ=1 AngleXU=0 Radius=6.1
  constraints (82):
    c: Equal(g4,g3)
    c: Equal(g3,g1)
    c: Equal(g1,g2)
    c: Diameter(g0) = 12.2
    c: Symmetric(g2,g4,g-2)
    c: DistanceX(g5) = -150
    c: DistanceY(g5) = 150
    c: DistanceY(g5,g2) = 10
    c: Vertical(g2,g1)
    c: Vertical(g1,g0)
    c: Symmetric(g6,g5,g-1)
    c: DistanceY(g6,g0) = 22
    c: DistanceX(g6,g0) = 9
    c: Vertical(g7,g6)
    c: Horizontal(g8,g1)
    c: DistanceY(g7,g8) = 19
    c: Symmetric(g3,g1,g-2)
    c: Vertical(g9)
    c: Vertical(g10)
    c: Horizontal(g10,g9)
    c: Horizontal(g9,g0)
    c: PointOnObject(g11,g0)
    c: Horizontal(g11,g0)
    c: DistanceX(g9,g11) = 0.75
    c: DistanceX(g9,g10) = 1.38
    c: Horizontal(g9,g10)
    c: Coincident(g13,g12)
    c: Coincident(g13,g9)
    c: Horizontal(g14)
    c: Horizontal(g15)
    c: Coincident(g16,g15)
    c: Coincident(g16,g14)
    c: Tangent(g15,g13) = 1.5708
    c: Coincident(g17,g0)
    c: Coincident(g17,g9)
    c: Coincident(g18,g17)
    c: Coincident(g18,g10)
    c: Vertical(g19)
    c: Vertical(g20)
    c: Tangent(g19,g17) = 1.5708
    c: Tangent(g20,g18) = -1.5708
    c: Coincident(g21,g2)
    c: Coincident(g22,g21)
    c: Tangent(g21,g19) = 1.5708
    c: Tangent(g22,g20) = -1.5708
    c: Horizontal(g23)
    c: Horizontal(g24)
    c: Tangent(g23,g21) = 1.5708
    c: Tangent(g24,g22) = -1.5708
    c: Coincident(g25,g4)
    c: Coincident(g26,g25)
    c: Tangent(g25,g23) = 1.5708
    c: Tangent(g26,g24) = -1.5708
    c: Vertical(g27)
    c: Vertical(g28)
    c: Tangent(g28,g26) = -1.5708
    c: Tangent(g27,g25) = 1.5708
    c: Coincident(g29,g3)
    c: Coincident(g30,g29)
    c: Tangent(g29,g27) = 1.5708
    c: Tangent(g30,g28) = -1.5708
    c: Horizontal(g31)
    c: Horizontal(g32)
    c: Tangent(g32,g29) = -1.5708
    c: Tangent(g31,g30) = 1.5708
    c: Coincident(g33,g32)
    c: Coincident(g33,g31)
    c: Vertical(g15,g31)
    c: Vertical(g16)
    c: Vertical(g33)
    c: DistanceX(g31) = 0
    c: Horizontal(g7,g34)
    c: Symmetric(g8,g12,g34)
    c: Vertical(g12,g8)
    c: DistanceY(g7) = 30
    c: Tangent(g14,g12) = 1.5708
    c: Coincident(g35,g12)
    c: Equal(g35,g1)
    c: Equal(g0,g1)
    c: Tangent(g12,g10) = -1.5708
    c: DistanceX(g7,g12) = 21.83
    c: PointOnObject(g12,g35)
FEATURE [PartDesign::Pad] Pad040
  Direction = (0,0,1)
  Length = 6
  Length2 = 10
  Midplane = true
  Profile = -> Sketch011
  ReferenceAxis = -> Sketch011 [N_Axis]
  Suppressed = false
  Type = 0
FEATURE [PartDesign::Body] Body021  label="xy-belt-1"
  AllowCompound = false
  Group = -> [Sketch011,Pad040]
  Origin = -> Origin021
  Placement = pos=(0,0,5) rot=(0,0,1;0rad)
  Tip = -> Pad040
FEATURE [Sketcher::SketchObject] Sketch254  label="belt-sketch001"
  ArcFitTolerance = 0
  AttachmentSupport = -> [XY_Plane255]
  FullyConstrained = true
  MakeInternals = false
  MapMode = 5
  expr: Constraints[76] = -Spreadsheet.x_position
  expr: Constraints[7] = -(Spreadsheet.side_length / 2 - 20)
  expr: Constraints[80] = Spreadsheet.y_position + 30
  expr: Constraints[8] = Spreadsheet.side_length / 2 - 20
  sketch-geometry (36):
    g0: Circle [constr] CenterX=-141 CenterY=-128 CenterZ=0 NormalX=0 NormalY=0 NormalZ=1 AngleXU=0 Radius=6.1
    g1: Circle [constr] CenterX=-128.17 CenterY=11 CenterZ=0 NormalX=0 NormalY=0 NormalZ=1 AngleXU=0 Radius=6.1
    g2: Circle [constr] CenterX=-141 CenterY=49 CenterZ=0 NormalX=0 NormalY=0 NormalZ=1 AngleXU=0 Radius=6.1
    g3: Circle [constr] CenterX=-141 CenterY=160 CenterZ=0 NormalX=0 NormalY=0 NormalZ=1 AngleXU=0 Radius=6.1
    g4: Circle [constr] CenterX=141 CenterY=49 CenterZ=0 NormalX=0 NormalY=0 NormalZ=1 AngleXU=0 Radius=6.1
    g5: Circle [constr] CenterX=141 CenterY=160 CenterZ=0 NormalX=0 NormalY=0 NormalZ=1 AngleXU=0 Radius=6.1
    g6: GeomPoint [constr] X=-150 Y=150 Z=0
    g7: GeomPoint [constr] X=-150 Y=-150 Z=0
    g8: GeomPoint [constr] X=-150 Y=30 Z=0
    g9: GeomPoint [constr] X=-128.17 Y=49 Z=0
    g10: LineSegment StartX=-135.65 StartY=-128 StartZ=0 EndX=-135.65 EndY=11 EndZ=0
    g11: LineSegment StartX=-134.27 StartY=11 StartZ=0 EndX=-134.27 EndY=-128 EndZ=0
    g12: GeomPoint [constr] X=-134.9 Y=-128 Z=0
    g13: ArcOfCircle CenterX=-128.17 CenterY=11 CenterZ=0 NormalX=0 NormalY=0 NormalZ=1 AngleXU=0 Radius=6.1 StartAngle=1.5708 EndAngle=3.14159
    g14: ArcOfCircle CenterX=-128.17 CenterY=11 CenterZ=0 NormalX=0 NormalY=0 NormalZ=1 AngleXU=0 Radius=7.48 StartAngle=1.5708 EndAngle=3.14159
    g15: LineSegment StartX=-128.17 StartY=17.1 StartZ=0 EndX=0 EndY=17.1 EndZ=0
    g16: LineSegment StartX=-128.17 StartY=18.48 StartZ=0 EndX=0 EndY=18.48 EndZ=0
    g17: LineSegment StartX=0 StartY=18.48 StartZ=0 EndX=0 EndY=17.1 EndZ=0
    g18: ArcOfCircle CenterX=-141 CenterY=-128 CenterZ=0 NormalX=0 NormalY=0 NormalZ=1 AngleXU=0 Radius=5.35 StartAngle=3.14159 EndAngle=6.28319
    g19: ArcOfCircle CenterX=-141 CenterY=-128 CenterZ=0 NormalX=0 NormalY=0 NormalZ=1 AngleXU=0 Radius=6.73 StartAngle=3.14159 EndAngle=6.28319
    g20: LineSegment StartX=-146.35 StartY=-128 StartZ=0 EndX=-146.35 EndY=160 EndZ=0
    g21: LineSegment StartX=-147.73 StartY=160 StartZ=0 EndX=-147.73 EndY=-128 EndZ=0
    g22: ArcOfCircle CenterX=-141 CenterY=160 CenterZ=0 NormalX=0 NormalY=0 NormalZ=1 AngleXU=0 Radius=5.35 StartAngle=1.5708 EndAngle=3.14159
    g23: ArcOfCircle CenterX=-141 CenterY=160 CenterZ=0 NormalX=0 NormalY=0 NormalZ=1 AngleXU=0 Radius=6.73 StartAngle=1.5708 EndAngle=3.14159
    g24: LineSegment StartX=-141 StartY=165.35 StartZ=0 EndX=141 EndY=165.35 EndZ=0
    g25: LineSegment StartX=141 StartY=166.73 StartZ=0 EndX=-141 EndY=166.73 EndZ=0
    g26: ArcOfCircle CenterX=141 CenterY=160 CenterZ=0 NormalX=0 NormalY=0 NormalZ=1 AngleXU=0 Radius=5.35 StartAngle=0 EndAngle=1.5708
    g27: ArcOfCircle CenterX=141 CenterY=160 CenterZ=0 NormalX=0 NormalY=0 NormalZ=1 AngleXU=0 Radius=6.73 StartAngle=-9e-16 EndAngle=1.5708
    g28: LineSegment StartX=146.35 StartY=160 StartZ=0 EndX=146.35 EndY=49 EndZ=0
    g29: LineSegment StartX=147.73 StartY=49 StartZ=0 EndX=147.73 EndY=160 EndZ=0
    g30: ArcOfCircle CenterX=141 CenterY=49 CenterZ=0 NormalX=0 NormalY=0 NormalZ=1 AngleXU=0 Radius=5.35 StartAngle=4.71239 EndAngle=6.28319
    g31: ArcOfCircle CenterX=141 CenterY=49 CenterZ=0 NormalX=0 NormalY=0 NormalZ=1 AngleXU=0 Radius=6.73 StartAngle=4.71239 EndAngle=6.28319
    g32: LineSegment StartX=141 StartY=42.27 StartZ=0 EndX=0 EndY=42.27 EndZ=0
    g33: LineSegment StartX=0 StartY=43.65 StartZ=0 EndX=141 EndY=43.65 EndZ=0
    g34: LineSegment StartX=0 StartY=43.65 StartZ=0 EndX=0 EndY=42.27 EndZ=0
    g35: GeomPoint [constr] X=-128.17 Y=30 Z=0
  constraints (83):
    c: Equal(g5,g4)
    c: Equal(g4,g2)
    c: Equal(g2,g3)
    c: Equal(g3,g1)
    c: Equal(g1,g0)
    c: Diameter(g0) = 12.2
    c: Symmetric(g3,g5,g-2)
    c: DistanceX(g6) = -150
    c: DistanceY(g6) = 150
    c: DistanceY(g6,g3) = 10
    c: Vertical(g3,g2)
    c: Vertical(g2,g0)
    c: Symmetric(g7,g6,g-1)
    c: DistanceY(g7,g0) = 22
    c: DistanceX(g7,g0) = 9
    c: Vertical(g8,g7)
    c: DistanceX(g8,g1) = 21.83
    c: Horizontal(g9,g2)
    c: DistanceY(g8,g9) = 19
    c: Symmetric(g4,g2,g-2)
    c: Vertical(g10)
    c: Vertical(g11)
    c: Horizontal(g11,g10)
    c: Horizontal(g10,g0)
    c: PointOnObject(g12,g0)
    c: Horizontal(g12,g0)
    c: DistanceX(g10,g12) = 0.75
    c: DistanceX(g10,g11) = 1.38
    c: Horizontal(g10,g11)
    c: Horizontal(g11,g1)
    c: Coincident(g13,g1)
    c: Coincident(g13,g11)
    c: Coincident(g14,g13)
    c: Coincident(g14,g10)
    c: Horizontal(g15)
    c: Horizontal(g16)
    c: Coincident(g17,g16)
    c: Coincident(g17,g15)
    c: Tangent(g16,g14) = 1.5708
    c: Coincident(g18,g0)
    c: Coincident(g18,g10)
    c: Coincident(g19,g18)
    c: Coincident(g19,g11)
    c: Vertical(g20)
    c: Vertical(g21)
    c: Tangent(g20,g18) = 1.5708
    c: Tangent(g21,g19) = -1.5708
    c: Coincident(g22,g3)
    c: Coincident(g23,g22)
    c: Tangent(g22,g20) = 1.5708
    c: Tangent(g23,g21) = -1.5708
    c: Horizontal(g24)
    c: Horizontal(g25)
    c: Tangent(g24,g22) = 1.5708
    c: Tangent(g25,g23) = -1.5708
    c: Coincident(g26,g5)
    c: Coincident(g27,g26)
    c: Tangent(g26,g24) = 1.5708
    c: Tangent(g27,g25) = -1.5708
    c: Vertical(g28)
    c: Vertical(g29)
    c: Tangent(g29,g27) = -1.5708
    c: Tangent(g28,g26) = 1.5708
    c: Coincident(g30,g4)
    c: Coincident(g31,g30)
    c: Tangent(g30,g28) = 1.5708
    c: Tangent(g31,g29) = -1.5708
    c: Horizontal(g32)
    c: Horizontal(g33)
    c: Tangent(g33,g30) = -1.5708
    c: Tangent(g32,g31) = 1.5708
    c: Coincident(g34,g33)
    c: Coincident(g34,g32)
    c: Vertical(g16,g32)
    c: Vertical(g17)
    c: Vertical(g34)
    c: DistanceX(g32) = 0
    c: Horizontal(g35,g8)
    c: Vertical(g9,g13)
    c: Symmetric(g13,g9,g35)
    c: DistanceY(g35) = 30
    c: Tangent(g15,g13) = 1.5708
    c: PointOnObject(g13,g1)
FEATURE [PartDesign::Pad] Pad059
  Direction = (0,0,1)
  Length = 6
  Length2 = 10
  Midplane = true
  Profile = -> Sketch254
  ReferenceAxis = -> Sketch254 [N_Axis]
  Suppressed = false
  Type = 0
FEATURE [PartDesign::Body] Body122  label="xy-belt-02"
  AllowCompound = false
  Group = -> [Sketch254,Pad059]
  Origin = -> Origin256
  Placement = pos=(0,0,-5) rot=(0,0,1;0rad)
  Tip = -> Pad059
FEATURE [PartDesign::FeatureBase] Clone014
  BaseFeature = -> Body153
  Suppressed = false
FEATURE [PartDesign::Body] Body155  label="rail-y-left"
  AllowCompound = false
  Group = -> [Clone014]
  Origin = -> Origin295
  Placement = pos=(-159.5,150,11) rot=(0,0,1;0rad)
  Tip = -> Clone014
  expr: .Placement.Base.x = -Spreadsheet.side_length / 2 + 10.5
  expr: .Placement.Base.y = Spreadsheet.side_length / 2 - 20
FEATURE [PartDesign::FeatureBase] Clone015
  BaseFeature = -> Body153
  Suppressed = false
FEATURE [PartDesign::Body] Body156  label="rail-y-right"
  AllowCompound = false
  Group = -> [Clone015]
  Origin = -> Origin296
  Placement = pos=(159.5,150,11) rot=(0,0,1;0rad)
  Tip = -> Clone015
  expr: .Placement.Base.x = Spreadsheet.side_length / 2 - 10.5
  expr: .Placement.Base.y = Spreadsheet.side_length / 2 - 20
FEATURE [Sketcher::SketchObject] Sketch477
  ArcFitTolerance = 1e-06
  AttachmentSupport = -> [XZ_Plane314]
  FullyConstrained = true
  MakeInternals = false
  MapMode = 5
  Placement = pos=(0,0,0) rot=(1,0,0;1.5708rad)
  sketch-geometry (9):
    g0: LineSegment StartX=-6 StartY=1 StartZ=0 EndX=-6 EndY=0 EndZ=0
    g1: LineSegment StartX=-6 StartY=0 StartZ=0 EndX=-4.41716 EndY=0 EndZ=0
    g2: LineSegment StartX=-4.41716 StartY=0 StartZ=0 EndX=-2.91716 EndY=-1.5 EndZ=0
    g3: LineSegment StartX=-2.91716 StartY=-1.5 StartZ=0 EndX=2.91716 EndY=-1.5 EndZ=0
    g4: LineSegment StartX=2.91716 StartY=-1.5 StartZ=0 EndX=4.41716 EndY=0 EndZ=0
    g5: LineSegment StartX=4.41716 StartY=0 StartZ=0 EndX=6 EndY=0 EndZ=0
    g6: LineSegment StartX=6 StartY=0 StartZ=0 EndX=6 EndY=1 EndZ=0
    g7: LineSegment StartX=6 StartY=1 StartZ=0 EndX=-6 EndY=1 EndZ=0
    g8: LineSegment [constr] StartX=-4.7 StartY=0 StartZ=0 EndX=-2.7 EndY=-2 EndZ=0
  constraints (26):
    c: Vertical(g0)
    c: Coincident(g0,g1)
    c: Horizontal(g1)
    c: Coincident(g1,g2)
    c: Coincident(g2,g3)
    c: Horizontal(g3)
    c: Coincident(g3,g4)
    c: PointOnObject(g4,g-1)
    c: Coincident(g4,g5)
    c: PointOnObject(g5,g-1)
    c: Coincident(g5,g6)
    c: Vertical(g6)
    c: Coincident(g6,g7)
    c: Coincident(g7,g0)
    c: Perpendicular(g2,g4)
    c: Angle(g4) = 0.785398
    c: Symmetric(g4,g1,g-1)
    c: Symmetric(g0,g6,g-2)
    c: DistanceY(g6,g6) = 1
    c: DistanceY(g2,g2) = 1.5
    c: PointOnObject(g8,g1)
    c: Parallel(g8,g2)
    c: DistanceY(g8,g8) = 2
    c: DistanceX(g8) = -2.7
    c: Distance(g1,g8) = 0.2
    c: DistanceX(g7,g7) = 12
FEATURE [PartDesign::Pad] Pad104
  Direction = (0,-1,2e-16)
  Length = 89.5
  Length2 = 30
  Placement = pos=(0,0,0) rot=(1,0,0;1.5708rad)
  Profile = -> Sketch477
  ReferenceAxis = -> Sketch477 [N_Axis]
  Suppressed = false
  Type = 4
FEATURE [PartDesign::Body] Body163  label="rail-spacer-y-left-front"
  AllowCompound = false
  Group = -> [Sketch477,Pad104]
  Origin = -> Origin315
  Placement = pos=(-160,0,10) rot=(0,0,1;0rad)
  Tip = -> Pad104
  expr: .Placement.Base.x = -Spreadsheet.side_length / 2 + 10
FEATURE [Sketcher::SketchObject] Sketch478
  ArcFitTolerance = 1e-06
  AttachmentSupport = -> [XZ_Plane315]
  FullyConstrained = true
  MakeInternals = false
  MapMode = 5
  Placement = pos=(0,0,0) rot=(1,0,0;1.5708rad)
  sketch-geometry (9):
    g0: LineSegment StartX=-6 StartY=1 StartZ=0 EndX=-6 EndY=0 EndZ=0
    g1: LineSegment StartX=-6 StartY=0 StartZ=0 EndX=-4.41716 EndY=0 EndZ=0
    g2: LineSegment StartX=-4.41716 StartY=0 StartZ=0 EndX=-2.91716 EndY=-1.5 EndZ=0
    g3: LineSegment StartX=-2.91716 StartY=-1.5 StartZ=0 EndX=2.91716 EndY=-1.5 EndZ=0
    g4: LineSegment StartX=2.91716 StartY=-1.5 StartZ=0 EndX=4.41716 EndY=0 EndZ=0
    g5: LineSegment StartX=4.41716 StartY=0 StartZ=0 EndX=6 EndY=0 EndZ=0
    g6: LineSegment StartX=6 StartY=0 StartZ=0 EndX=6 EndY=1 EndZ=0
    g7: LineSegment StartX=6 StartY=1 StartZ=0 EndX=-6 EndY=1 EndZ=0
    g8: LineSegment [constr] StartX=-4.7 StartY=0 StartZ=0 EndX=-2.7 EndY=-2 EndZ=0
  constraints (26):
    c: Vertical(g0)
    c: Coincident(g0,g1)
    c: Horizontal(g1)
    c: Coincident(g1,g2)
    c: Coincident(g2,g3)
    c: Horizontal(g3)
    c: Coincident(g3,g4)
    c: PointOnObject(g4,g-1)
    c: Coincident(g4,g5)
    c: PointOnObject(g5,g-1)
    c: Coincident(g5,g6)
    c: Vertical(g6)
    c: Coincident(g6,g7)
    c: Coincident(g7,g0)
    c: Perpendicular(g2,g4)
    c: Angle(g4) = 0.785398
    c: Symmetric(g4,g1,g-1)
    c: Symmetric(g0,g6,g-2)
    c: DistanceY(g6,g6) = 1
    c: DistanceY(g2,g2) = 1.5
    c: PointOnObject(g8,g1)
    c: Parallel(g8,g2)
    c: DistanceY(g8,g8) = 2
    c: DistanceX(g8) = -2.7
    c: Distance(g1,g8) = 0.2
    c: DistanceX(g7,g7) = 12
FEATURE [PartDesign::Pad] Pad105
  Direction = (0,-1,2e-16)
  Length = 149.5
  Length2 = -30
  Placement = pos=(0,0,0) rot=(1,0,0;1.5708rad)
  Profile = -> Sketch478
  ReferenceAxis = -> Sketch478 [N_Axis]
  Reversed = true
  Suppressed = false
  Type = 4
FEATURE [PartDesign::Body] Body164  label="rail-spacer-y-left-back"
  AllowCompound = false
  Group = -> [Sketch478,Pad105]
  Origin = -> Origin316
  Placement = pos=(-160,0,10) rot=(0,0,1;0rad)
  Tip = -> Pad105
  expr: .Placement.Base.x = -Spreadsheet.side_length / 2 + 10
COMPONENT P15 — recipe-attached ("z-motion-back-idler-mount-left", modeled in this document).
Construction recipe (the document's own serialized feature program — sketch geometry with constraints, then the solid features built on it; lengths are millimeters unless a unit is written):

FEATURE [PartDesign::PolarPattern] PolarPattern002
  Angle = 360
  Axis = -> Z_Axis260
  Mode = 0
  Occurrences = 4
  Offset = 120
  Suppressed = false
  TransformMode = 0
FEATURE [Sketcher::SketchObject] Sketch256
  ArcFitTolerance = 0
  AttachmentSupport = -> [XY_Plane260]
  FullyConstrained = true
  MakeInternals = false
  MapMode = 5
  sketch-geometry (22):
    g0: ArcOfCircle CenterX=-9 CenterY=9 CenterZ=0 NormalX=0 NormalY=0 NormalZ=1 AngleXU=0 Radius=1 StartAngle=1.5708 EndAngle=2.35619
    g1: LineSegment StartX=-9 StartY=10 StartZ=0 EndX=-4.90355 EndY=10 EndZ=0
    g2: LineSegment StartX=-4.55 StartY=9.85355 StartZ=0 EndX=-3.12322 EndY=8.42678 EndZ=0
    g3: LineSegment StartX=-3.3 StartY=8 StartZ=0 EndX=-5.75 EndY=8 EndZ=0
    g4: LineSegment StartX=-5.85355 StartY=6.91421 StartZ=0 EndX=-3.08579 EndY=4.14645 EndZ=0
    g5: LineSegment StartX=-2.73223 StartY=4 StartZ=0 EndX=0 EndY=4 EndZ=0
    g6: LineSegment StartX=-6 StartY=7.75 StartZ=0 EndX=-6 EndY=7.26777 EndZ=0
    g7: ArcOfCircle CenterX=-3.3 CenterY=8.25 CenterZ=0 NormalX=0 NormalY=0 NormalZ=1 AngleXU=0 Radius=0.25 StartAngle=4.71239 EndAngle=7.06858
    g8: ArcOfCircle CenterX=-4.90355 CenterY=9.5 CenterZ=0 NormalX=0 NormalY=0 NormalZ=1 AngleXU=0 Radius=0.5 StartAngle=0.785398 EndAngle=1.5708
    g9: GeomPoint [constr] X=-3.05 Y=8.25 Z=0
    g10: ArcOfCircle CenterX=-2.73223 CenterY=4.5 CenterZ=0 NormalX=0 NormalY=0 NormalZ=1 AngleXU=0 Radius=0.5 StartAngle=3.92699 EndAngle=4.71239
    g11: GeomPoint [constr] X=-2.93934 Y=4 Z=0
    g12: ArcOfCircle CenterX=-5.5 CenterY=7.26777 CenterZ=0 NormalX=0 NormalY=0 NormalZ=1 AngleXU=0 Radius=0.5 StartAngle=3.14159 EndAngle=3.92699
    g13: GeomPoint [constr] X=-6 Y=7.06066 Z=0
    g14: ArcOfCircle CenterX=-5.75 CenterY=7.75 CenterZ=0 NormalX=0 NormalY=0 NormalZ=1 AngleXU=0 Radius=0.25 StartAngle=1.5708 EndAngle=3.14159
    g15: GeomPoint [constr] X=-6 Y=8 Z=0
    g16: ArcOfCircle CenterX=0 CenterY=0 CenterZ=0 NormalX=0 NormalY=0 NormalZ=1 AngleXU=0 Radius=2.75 StartAngle=1.5708 EndAngle=2.35619
    g17: GeomPoint [constr] X=0 Y=10 Z=0
    g18: GeomPoint [constr] X=-10 Y=10 Z=0
    g19: LineSegment StartX=-9.70711 StartY=9.70711 StartZ=0 EndX=-1.94454 EndY=1.94454 EndZ=0
    g20: LineSegment StartX=2e-16 StartY=2.75 StartZ=0 EndX=0 EndY=4 EndZ=0
    g21: LineSegment [constr] StartX=-4.46967 StartY=5.53033 StartZ=0 EndX=-5 EndY=5 EndZ=0
  constraints (55):
    c: Radius(g0) = 1
    c: Horizontal(g3)
    c: Parallel(g2,g4)
    c: Vertical(g6)
    c: Tangent(g2,g7) = 1.5708
    c: Tangent(g3,g7) = 1.5708
    c: Tangent(g1,g8) = 1.5708
    c: Tangent(g2,g8) = 1.5708
    c: Radius(g7) = 0.25
    c: Tangent(g1,g0) = 1.5708
    c: PointOnObject(g9,g7)
    c: Horizontal(g9,g7)
    c: PointOnObject(g11,g4)
    c: PointOnObject(g11,g5)
    c: Tangent(g4,g10) = -1.5708
    c: Tangent(g5,g10) = -1.5708
    c: PointOnObject(g13,g4)
    c: PointOnObject(g13,g6)
    c: Tangent(g4,g12) = -1.5708
    c: Tangent(g6,g12) = -1.5708
    c: PointOnObject(g15,g3)
    c: PointOnObject(g15,g6)
    c: Tangent(g3,g14) = -1.5708
    c: Tangent(g6,g14) = -1.5708
    c: Equal(g10,g12)
    c: PointOnObject(g5,g-2)
    c: Coincident(g16,g-1)
    c: PointOnObject(g16,g-2)
    c: PointOnObject(g17,g-2)
    c: PointOnObject(g17,g1)
    c: PointOnObject(g18,g1)
    c: Coincident(g19,g0)
    c: Coincident(g16,g19)
    c: PointOnObject(g0,g19)
    c: PointOnObject(g18,g19)
    c: Parallel(g19,g4)
    c: DistanceX(g18) = -10
    c: DistanceY(g18) = 10
    c: PointOnObject(g16,g19)
    c: Horizontal(g5)
    c: Coincident(g20,g16)
    c: Coincident(g20,g5)
    c: Horizontal(g1)
    c: DistanceX(g15) = -6
    c: DistanceX(g9) = -3.05
    c: DistanceY(g3,g1) = 2
    c: Radius(g10) = 0.5
    c: Radius(g16) = 2.75
    c: DistanceY(g5) = 4
    c: PointOnObject(g21,g4)
    c: Perpendicular(g19,g21)
    c: Distance(g21) = 0.75
    c: Symmetric(g16,g18,g21)
    c: Equal(g14,g7)
    c: Equal(g8,g12)
FEATURE [PartDesign::Mirrored] Mirrored008
  MirrorPlane = -> Sketch256 [V_Axis]
  Suppressed = false
  TransformMode = 0
FEATURE [PartDesign::Pad] Pad061
  Direction = (0,0,1)
  Length = 265
  Length2 = 10
  Midplane = true
  Profile = -> Sketch256
  ReferenceAxis = -> Sketch256 [N_Axis]
  Suppressed = false
  Type = 0
  expr: Length = Spreadsheet.side_length - 75
FEATURE [PartDesign::MultiTransform] MultiTransform004
  BaseFeature = -> Pad061
  Originals = -> [Pad061]
  Refine = true
  Suppressed = false
  TransformMode = 0
  Transformations = -> [Mirrored008,PolarPattern002]
FEATURE [PartDesign::Body] Body126  label="extrusion-left"
  AllowCompound = false
  Group = -> [Sketch256,Pad061,MultiTransform004,Mirrored008,PolarPattern002]
  Origin = -> Origin261
  Placement = pos=(-140,-2.5,0) rot=(1,0,0;1.5708rad)
  Tip = -> MultiTransform004
  expr: .Placement.Base.x = -Spreadsheet.side_length / 2 + 30
FEATURE [Sketcher::SketchObject] Sketch259
  ArcFitTolerance = 1e-06
  AttachmentSupport = -> [XY_Plane263]
  FullyConstrained = true
  MakeInternals = false
  MapMode = 5
  expr: Constraints[11] = -Spreadsheet.side_length / 2 + 74
  expr: Constraints[6] = -Spreadsheet.side_length / 2 + 30
  expr: Constraints[9] = -Spreadsheet.bed_hole_distance / 2 + 14
  sketch-geometry (15):
    g0: LineSegment StartX=-152.5 StartY=-37 StartZ=0 EndX=-101.5 EndY=-37 EndZ=0
    g1: LineSegment StartX=-100 StartY=-38.5 StartZ=0 EndX=-100 EndY=-65 EndZ=0
    g2: LineSegment StartX=-100 StartY=-65 StartZ=0 EndX=-131 EndY=-96 EndZ=0
    g3: LineSegment StartX=-131 StartY=-96 StartZ=0 EndX=-152.5 EndY=-96 EndZ=0
    g4: LineSegment StartX=-154 StartY=-94.5 StartZ=0 EndX=-154 EndY=-38.5 EndZ=0
    g5: GeomPoint X=-140 Y=-51 Z=0
    g6: GeomPoint X=-140 Y=-96 Z=0
    g7: GeomPoint X=-100 Y=-51 Z=0
    g8: GeomPoint X=-130 Y=-51 Z=0
    g9: ArcOfCircle CenterX=-152.5 CenterY=-38.5 CenterZ=0 NormalX=0 NormalY=0 NormalZ=1 AngleXU=0 Radius=1.5 StartAngle=1.5708 EndAngle=3.14159
    g10: GeomPoint [constr] X=-154 Y=-37 Z=0
    g11: ArcOfCircle CenterX=-101.5 CenterY=-38.5 CenterZ=0 NormalX=0 NormalY=0 NormalZ=1 AngleXU=0 Radius=1.5 StartAngle=1.5e-15 EndAngle=1.5708
    g12: GeomPoint [constr] X=-100 Y=-37 Z=0
    g13: ArcOfCircle CenterX=-152.5 CenterY=-94.5 CenterZ=0 NormalX=0 NormalY=0 NormalZ=1 AngleXU=0 Radius=1.5 StartAngle=3.14159 EndAngle=4.71239
    g14: GeomPoint [constr] X=-154 Y=-96 Z=0
  constraints (34):
    c: Horizontal(g0)
    c: Vertical(g1)
    c: Coincident(g1,g2)
    c: Coincident(g2,g3)
    c: Horizontal(g3)
    c: Vertical(g4)
    c: DistanceX(g5) = -140
    c: Vertical(g6,g5)
    c: Symmetric(g12,g1,g7)
    c: DistanceY(g5) = -51
    c: Horizontal(g7,g5)
    c: DistanceY(g2) = -96
    c: DistanceX(g14,g6) = 14
    c: Angle(g2) = -2.35619
    c: DistanceY(g1,g12) = 28
    c: Horizontal(g8,g5)
    c: DistanceX(g5,g8) = 10
    c: DistanceX(g8,g7) = 30
    c: PointOnObject(g6,g3)
    c: PointOnObject(g10,g0)
    c: PointOnObject(g10,g4)
    c: Tangent(g0,g9) = 1.5708
    c: Tangent(g4,g9) = 1.5708
    c: PointOnObject(g12,g1)
    c: PointOnObject(g12,g0)
    c: Tangent(g1,g11) = 1.5708
    c: Tangent(g0,g11) = 1.5708
    c: PointOnObject(g14,g3)
    c: PointOnObject(g14,g4)
    c: Tangent(g3,g13) = 1.5708
    c: Tangent(g4,g13) = 1.5708
    c: Equal(g13,g9)
    c: Equal(g9,g11)
    c: Radius(g11) = 1.5
FEATURE [PartDesign::Pad] Pad063
  Direction = (0,0,1)
  Length = 28
  Length2 = 10
  Midplane = true
  Profile = -> Sketch259
  ReferenceAxis = -> Sketch259 [N_Axis]
  Suppressed = false
  Type = 0
FEATURE [Sketcher::SketchObject] Sketch260
  ArcFitTolerance = 1e-06
  AttachmentSupport = -> [XY_Plane263]
  FullyConstrained = true
  MakeInternals = false
  MapMode = 5
  expr: Constraints[0] = -Spreadsheet.side_length / 2 + 30
  expr: Constraints[1] = -Spreadsheet.bed_hole_distance / 2 + 14
  expr: Constraints[26] = -Spreadsheet.side_length / 2 + 74
  sketch-geometry (11):
    g0: GeomPoint X=-140 Y=-51 Z=0
    g1: LineSegment StartX=-150.05 StartY=-37 StartZ=0 EndX=-129.95 EndY=-37 EndZ=0
    g2: LineSegment StartX=-129.95 StartY=-37 StartZ=0 EndX=-129.95 EndY=-40.95 EndZ=0
    g3: LineSegment StartX=-129.95 StartY=-40.95 StartZ=0 EndX=-100 EndY=-40.95 EndZ=0
    g4: LineSegment StartX=-100 StartY=-40.95 StartZ=0 EndX=-100 EndY=-61.05 EndZ=0
    g5: LineSegment StartX=-100 StartY=-61.05 StartZ=0 EndX=-129.95 EndY=-61.05 EndZ=0
    g6: LineSegment StartX=-129.95 StartY=-61.05 StartZ=0 EndX=-129.95 EndY=-96 EndZ=0
    g7: LineSegment StartX=-129.95 StartY=-96 StartZ=0 EndX=-150.05 EndY=-96 EndZ=0
    g8: LineSegment StartX=-150.05 StartY=-96 StartZ=0 EndX=-150.05 EndY=-37 EndZ=0
    g9: GeomPoint X=-140 Y=-37 Z=0
    g10: GeomPoint X=-100 Y=-51 Z=0
  constraints (28):
    c: DistanceX(g0) = -140
    c: DistanceY(g0) = -51
    c: Horizontal(g1)
    c: Coincident(g1,g2)
    c: Vertical(g2)
    c: Coincident(g2,g3)
    c: Horizontal(g3)
    c: Coincident(g3,g4)
    c: Vertical(g4)
    c: Coincident(g4,g5)
    c: Horizontal(g5)
    c: Coincident(g5,g6)
    c: Vertical(g6)
    c: Coincident(g6,g7)
    c: Horizontal(g7)
    c: Coincident(g7,g8)
    c: Coincident(g8,g1)
    c: Vertical(g8)
    c: Symmetric(g1,g1,g9)
    c: Vertical(g9,g0)
    c: DistanceX(g1,g1) = 20.1
    c: Equal(g1,g4)
    c: Vertical(g5,g2)
    c: Symmetric(g4,g4,g10)
    c: Horizontal(g10,g0)
    c: DistanceX(g0,g3) = 40
    c: DistanceY(g6) = -96
    c: DistanceY(g0,g1) = 14
FEATURE [PartDesign::Pocket] Pocket
  BaseFeature = -> Pad063
  Direction = (0,0,-1)
  Length = 20.1
  Length2 = 5
  Midplane = true
  Profile = -> Sketch260
  ReferenceAxis = -> Sketch260 [N_Axis]
  Suppressed = false
  Type = 0
FEATURE [Sketcher::SketchObject] Sketch261
  ArcFitTolerance = 1e-06
  AttachmentSupport = -> [XY_Plane263]
  FullyConstrained = true
  MakeInternals = false
  MapMode = 5
  expr: Constraints[0] = -Spreadsheet.bed_hole_distance / 2 + 14
  expr: Constraints[1] = -Spreadsheet.side_length / 2 + 30
  expr: Constraints[9] = -Spreadsheet.side_length / 2 + 74
  sketch-geometry (5):
    g0: GeomPoint X=-140 Y=-51 Z=0
    g1: Circle CenterX=-115 CenterY=-51 CenterZ=0 NormalX=0 NormalY=0 NormalZ=1 AngleXU=0 Radius=2.75
    g2: Circle CenterX=-140 CenterY=-66.5 CenterZ=0 NormalX=0 NormalY=0 NormalZ=1 AngleXU=0 Radius=2.75
    g3: GeomPoint X=-140 Y=-37 Z=0
    g4: GeomPoint X=-140 Y=-96 Z=0
  constraints (11):
    c: DistanceY(g0) = -51
    c: DistanceX(g0) = -140
    c: Horizontal(g1,g0)
    c: Vertical(g0,g2)
    c: Equal(g1,g2)
    c: Diameter(g1) = 5.5
    c: DistanceX(g0,g1) = 25
    c: Vertical(g3,g0)
    c: DistanceY(g0,g3) = 14
    c: DistanceY(g4) = -96
    c: Symmetric(g3,g4,g2)
FEATURE [PartDesign::Pocket] Pocket001
  BaseFeature = -> Pocket
  Direction = (0,0,-1)
  Length = 5
  Length2 = 5
  Profile = -> Sketch261
  ReferenceAxis = -> Sketch261 [N_Axis]
  Reversed = true
  Suppressed = false
  Type = 1
FEATURE [PartDesign::Chamfer] Chamfer
  Angle = 45
  Base = -> Pocket001 [Edge25]
  BaseFeature = -> Pocket001
  ChamferType = 1
  FlipDirection = true
  Size = 4
  Size2 = 1
  SupportTransform = false
  Suppressed = false
  UseAllEdges = false
FEATURE [PartDesign::Chamfer] Chamfer001
  Angle = 45
  Base = -> Chamfer [Edge51]
  BaseFeature = -> Chamfer
  ChamferType = 1
  FlipDirection = false
  Size = 4
  Size2 = 1
  SupportTransform = false
  Suppressed = false
  UseAllEdges = false
FEATURE [PartDesign::Chamfer] Chamfer002
  Angle = 45
  Base = -> Chamfer001 [Edge44]
  BaseFeature = -> Chamfer001
  ChamferType = 1
  FlipDirection = false
  Size = 4
  Size2 = 1
  SupportTransform = false
  Suppressed = false
  UseAllEdges = false
FEATURE [PartDesign::Fillet] Fillet
  Base = -> Chamfer002 [Edge41,Edge18,Edge45]
  BaseFeature = -> Chamfer002
  Radius = 8
  SupportTransform = false
  Suppressed = false
  UseAllEdges = false
FEATURE [PartDesign::Fillet] Fillet001
  Base = -> Fillet [Edge42,Edge41]
  BaseFeature = -> Fillet
  Radius = 1.5
  SupportTransform = false
  Suppressed = false
  UseAllEdges = false
FEATURE [Sketcher::SketchObject] Sketch262
  ArcFitTolerance = 1e-06
  AttachmentSupport = -> [XY_Plane264]
  FullyConstrained = true
  MakeInternals = false
  MapMode = 5
  expr: Constraints[0] = Spreadsheet.bed_hole_distance / 2 + 14
  expr: Constraints[16] = Spreadsheet.side_length / 2 - 60
  expr: Constraints[1] = -Spreadsheet.side_length / 2 + 30
  sketch-geometry (14):
    g0: GeomPoint X=-140 Y=79 Z=0
    g1: LineSegment StartX=-152.5 StartY=110 StartZ=0 EndX=-117 EndY=110 EndZ=0
    g2: LineSegment StartX=-117 StartY=110 StartZ=0 EndX=-100 EndY=93 EndZ=0
    g3: LineSegment StartX=-100 StartY=93 StartZ=0 EndX=-100 EndY=66.5 EndZ=0
    g4: LineSegment StartX=-101.5 StartY=65 StartZ=0 EndX=-152.5 EndY=65 EndZ=0
    g5: LineSegment StartX=-154 StartY=66.5 StartZ=0 EndX=-154 EndY=108.5 EndZ=0
    g6: GeomPoint X=-100 Y=79 Z=0
    g7: GeomPoint X=-140 Y=110 Z=0
    g8: ArcOfCircle CenterX=-152.5 CenterY=108.5 CenterZ=0 NormalX=0 NormalY=0 NormalZ=1 AngleXU=0 Radius=1.5 StartAngle=1.5708 EndAngle=3.14159
    g9: GeomPoint [constr] X=-154 Y=110 Z=0
    g10: ArcOfCircle CenterX=-152.5 CenterY=66.5 CenterZ=0 NormalX=0 NormalY=0 NormalZ=1 AngleXU=0 Radius=1.5 StartAngle=3.14159 EndAngle=4.71239
    g11: GeomPoint [constr] X=-154 Y=65 Z=0
    g12: ArcOfCircle CenterX=-101.5 CenterY=66.5 CenterZ=0 NormalX=0 NormalY=0 NormalZ=1 AngleXU=0 Radius=1.5 StartAngle=4.71239 EndAngle=6.28319
    g13: GeomPoint [constr] X=-100 Y=65 Z=0
  constraints (32):
    c: DistanceY(g0) = 79
    c: DistanceX(g0) = -140
    c: Horizontal(g1)
    c: Coincident(g1,g2)
    c: Coincident(g2,g3)
    c: Vertical(g3)
    c: Horizontal(g4)
    c: Vertical(g5)
    c: Symmetric(g3,g13,g6)
    c: PointOnObject(g7,g1)
    c: DistanceX(g9,g7) = 14
    c: Vertical(g7,g0)
    c: Horizontal(g0,g6)
    c: Angle(g2) = -0.785398
    c: DistanceY(g13,g3) = 28
    c: DistanceX(g0,g6) = 40
    c: DistanceY(g7) = 110
    c: PointOnObject(g9,g1)
    c: PointOnObject(g9,g5)
    c: Tangent(g1,g8) = 1.5708
    c: Tangent(g5,g8) = 1.5708
    c: PointOnObject(g11,g4)
    c: PointOnObject(g11,g5)
    c: Tangent(g4,g10) = 1.5708
    c: Tangent(g5,g10) = 1.5708
    c: PointOnObject(g13,g3)
    c: PointOnObject(g13,g4)
    c: Tangent(g3,g12) = 1.5708
    c: Tangent(g4,g12) = 1.5708
    c: Equal(g8,g10)
    c: Equal(g10,g12)
    c: Radius(g10) = 1.5
FEATURE [PartDesign::Pad] Pad064
  Direction = (0,0,1)
  Length = 28
  Length2 = 10
  Midplane = true
  Profile = -> Sketch262
  ReferenceAxis = -> Sketch262 [N_Axis]
  Suppressed = false
  Type = 0
FEATURE [Sketcher::SketchObject] Sketch263
  ArcFitTolerance = 1e-06
  AttachmentSupport = -> [XY_Plane264]
  FullyConstrained = true
  MakeInternals = false
  MapMode = 5
  expr: Constraints[0] = -Spreadsheet.side_length / 2 + 30
  expr: Constraints[1] = Spreadsheet.bed_hole_distance / 2 + 14
  expr: Constraints[22] = Spreadsheet.side_length / 2 - 60
  sketch-geometry (11):
    g0: GeomPoint X=-140 Y=79 Z=0
    g1: LineSegment StartX=-150.05 StartY=110 StartZ=0 EndX=-150.05 EndY=65 EndZ=0
    g2: LineSegment StartX=-150.05 StartY=65 StartZ=0 EndX=-129.95 EndY=65 EndZ=0
    g3: LineSegment StartX=-129.95 StartY=65 StartZ=0 EndX=-129.95 EndY=68.95 EndZ=0
    g4: LineSegment StartX=-129.95 StartY=68.95 StartZ=0 EndX=-100 EndY=68.95 EndZ=0
    g5: LineSegment StartX=-100 StartY=68.95 StartZ=0 EndX=-100 EndY=89.05 EndZ=0
    g6: LineSegment StartX=-100 StartY=89.05 StartZ=0 EndX=-129.95 EndY=89.05 EndZ=0
    g7: LineSegment StartX=-129.95 StartY=89.05 StartZ=0 EndX=-129.95 EndY=110 EndZ=0
    g8: LineSegment StartX=-129.95 StartY=110 StartZ=0 EndX=-150.05 EndY=110 EndZ=0
    g9: GeomPoint X=-140 Y=65 Z=0
    g10: GeomPoint X=-100 Y=79 Z=0
  constraints (28):
    c: DistanceX(g0) = -140
    c: DistanceY(g0) = 79
    c: Vertical(g1)
    c: Coincident(g1,g2)
    c: Horizontal(g2)
    c: Coincident(g2,g3)
    c: Vertical(g3)
    c: Coincident(g3,g4)
    c: Horizontal(g4)
    c: Coincident(g4,g5)
    c: Vertical(g5)
    c: Coincident(g5,g6)
    c: Horizontal(g6)
    c: Coincident(g6,g7)
    c: Vertical(g7)
    c: Coincident(g7,g8)
    c: Coincident(g8,g1)
    c: Horizontal(g8)
    c: Vertical(g6,g3)
    c: Symmetric(g2,g2,g9)
    c: Vertical(g9,g0)
    c: DistanceY(g9,g0) = 14
    c: DistanceY(g7) = 110
    c: DistanceX(g2,g2) = 20.1
    c: Equal(g8,g5)
    c: DistanceX(g0,g4) = 40
    c: Symmetric(g5,g5,g10)
    c: Horizontal(g0,g10)
FEATURE [PartDesign::Pocket] Pocket002
  BaseFeature = -> Pad064
  Direction = (0,0,-1)
  Length = 20.1
  Length2 = 5
  Midplane = true
  Profile = -> Sketch263
  ReferenceAxis = -> Sketch263 [N_Axis]
  Suppressed = false
  Type = 0
FEATURE [PartDesign::Chamfer] Chamfer003
  Angle = 45
  Base = -> Pocket002 [Edge33]
  BaseFeature = -> Pocket002
  ChamferType = 1
  FlipDirection = false
  Size = 1
  Size2 = 4
  SupportTransform = false
  Suppressed = false
  UseAllEdges = false
FEATURE [PartDesign::Chamfer] Chamfer004
  Angle = 45
  Base = -> Chamfer003 [Edge48]
  BaseFeature = -> Chamfer003
  ChamferType = 1
  FlipDirection = false
  Size = 1
  Size2 = 4
  SupportTransform = false
  Suppressed = false
  UseAllEdges = false
FEATURE [PartDesign::Chamfer] Chamfer005
  Angle = 45
  Base = -> Chamfer004 [Edge14]
  BaseFeature = -> Chamfer004
  ChamferType = 1
  FlipDirection = false
  Size = 4
  Size2 = 1
  SupportTransform = false
  Suppressed = false
  UseAllEdges = false
FEATURE [PartDesign::Fillet] Fillet002
  Base = -> Chamfer005 [Edge42,Edge16,Edge15]
  BaseFeature = -> Chamfer005
  Radius = 8
  SupportTransform = false
  Suppressed = false
  UseAllEdges = false
FEATURE [PartDesign::Fillet] Fillet003
  Base = -> Fillet002 [Edge31,Edge8,Edge38,Edge9,Edge53,Edge14,Edge64,Edge68]
  BaseFeature = -> Fillet002
  Radius = 1.5
  SupportTransform = false
  Suppressed = false
  UseAllEdges = false
FEATURE [Sketcher::SketchObject] Sketch264
  ArcFitTolerance = 1e-06
  AttachmentSupport = -> [XY_Plane264]
  FullyConstrained = true
  MakeInternals = false
  MapMode = 5
  expr: Constraints[0] = -Spreadsheet.side_length / 2 + 30
  expr: Constraints[1] = Spreadsheet.bed_hole_distance / 2 + 14
  expr: Constraints[9] = Spreadsheet.side_length / 2 - 60
  sketch-geometry (5):
    g0: GeomPoint X=-140 Y=79 Z=0
    g1: GeomPoint X=-140 Y=110 Z=0
    g2: GeomPoint X=-140 Y=65 Z=0
    g3: Circle CenterX=-115 CenterY=79 CenterZ=0 NormalX=0 NormalY=0 NormalZ=1 AngleXU=0 Radius=2.75
    g4: Circle CenterX=-140 CenterY=87.5 CenterZ=0 NormalX=0 NormalY=0 NormalZ=1 AngleXU=0 Radius=2.75
  constraints (11):
    c: DistanceX(g0) = -140
    c: DistanceY(g0) = 79
    c: Vertical(g2,g0)
    c: Vertical(g0,g1)
    c: Equal(g4,g3)
    c: Diameter(g4) = 5.5
    c: Symmetric(g2,g1,g4)
    c: Horizontal(g3,g0)
    c: DistanceX(g0,g3) = 25
    c: DistanceY(g1) = 110
    c: DistanceY(g2,g0) = 14
FEATURE [PartDesign::Pocket] Pocket003
  BaseFeature = -> Fillet003
  Direction = (0,0,-1)
  Length = 5
  Length2 = 5
  Profile = -> Sketch264
  ReferenceAxis = -> Sketch264 [N_Axis]
  Refine = true
  Reversed = true
  Suppressed = false
  Type = 1
FEATURE [PartDesign::Body] Body129  label="bed-extrusion-connection-back-left"
  AllowCompound = false
  Group = -> [Sketch262,Pad064,Sketch263,Pocket002,Chamfer003,Chamfer004,Chamfer005,Fillet002,Fillet003,Sketch264,Pocket003]
  Origin = -> Origin265
  Tip = -> Pocket003
FEATURE [PartDesign::Fillet] Fillet009
  Base = -> Fillet001 [Edge28,Edge49,Edge56,Edge36]
  BaseFeature = -> Fillet001
  Radius = 1
  SupportTransform = false
  Suppressed = false
  UseAllEdges = false
FEATURE [PartDesign::Body] Body128  label="bed-extrusion-connection-front-left"
  AllowCompound = false
  Group = -> [Sketch259,Pad063,Sketch260,Pocket,Sketch261,Pocket001,Chamfer,Chamfer001,Chamfer002,Fillet,Fillet001,Fillet009]
  Origin = -> Origin264
  Tip = -> Fillet009
COMPONENT P16 — same part as P14; its construction recipe is shown at P14.
COMPONENT P17 — same part as P14; its construction recipe is shown at P14.
COMPONENT P18 — same part as P14; its construction recipe is shown at P14.
COMPONENT P19 — same part as P14; its construction recipe is shown at P14.
COMPONENT P20 — same part as P14; its construction recipe is shown at P14.
COMPONENT P21 — same part as P14; its construction recipe is shown at P14.
COMPONENT P22 — recipe-attached ("mainboard", modeled in this document).
Construction recipe (the document's own serialized feature program — sketch geometry with constraints, then the solid features built on it; lengths are millimeters unless a unit is written):

FEATURE [Sketcher::SketchObject] Sketch
  ArcFitTolerance = 0
  AttachmentSupport = -> [XY_Plane005]
  FullyConstrained = true
  MakeInternals = false
  MapMode = 5
  sketch-geometry (22):
    g0: ArcOfCircle CenterX=-9 CenterY=9 CenterZ=0 NormalX=0 NormalY=0 NormalZ=1 AngleXU=0 Radius=1 StartAngle=1.5708 EndAngle=2.35619
    g1: LineSegment StartX=-9 StartY=10 StartZ=0 EndX=-4.90355 EndY=10 EndZ=0
    g2: LineSegment StartX=-4.55 StartY=9.85355 StartZ=0 EndX=-3.12322 EndY=8.42678 EndZ=0
    g3: LineSegment StartX=-3.3 StartY=8 StartZ=0 EndX=-5.75 EndY=8 EndZ=0
    g4: LineSegment StartX=-5.85355 StartY=6.91421 StartZ=0 EndX=-3.08579 EndY=4.14645 EndZ=0
    g5: LineSegment StartX=-2.73223 StartY=4 StartZ=0 EndX=0 EndY=4 EndZ=0
    g6: LineSegment StartX=-6 StartY=7.75 StartZ=0 EndX=-6 EndY=7.26777 EndZ=0
    g7: ArcOfCircle CenterX=-3.3 CenterY=8.25 CenterZ=0 NormalX=0 NormalY=0 NormalZ=1 AngleXU=0 Radius=0.25 StartAngle=4.71239 EndAngle=7.06858
    g8: ArcOfCircle CenterX=-4.90355 CenterY=9.5 CenterZ=0 NormalX=0 NormalY=0 NormalZ=1 AngleXU=0 Radius=0.5 StartAngle=0.785398 EndAngle=1.5708
    g9: GeomPoint [constr] X=-3.05 Y=8.25 Z=0
    g10: ArcOfCircle CenterX=-2.73223 CenterY=4.5 CenterZ=0 NormalX=0 NormalY=0 NormalZ=1 AngleXU=0 Radius=0.5 StartAngle=3.92699 EndAngle=4.71239
    g11: GeomPoint [constr] X=-2.93934 Y=4 Z=0
    g12: ArcOfCircle CenterX=-5.5 CenterY=7.26777 CenterZ=0 NormalX=0 NormalY=0 NormalZ=1 AngleXU=0 Radius=0.5 StartAngle=3.14159 EndAngle=3.92699
    g13: GeomPoint [constr] X=-6 Y=7.06066 Z=0
    g14: ArcOfCircle CenterX=-5.75 CenterY=7.75 CenterZ=0 NormalX=0 NormalY=0 NormalZ=1 AngleXU=0 Radius=0.25 StartAngle=1.5708 EndAngle=3.14159
    g15: GeomPoint [constr] X=-6 Y=8 Z=0
    g16: ArcOfCircle CenterX=0 CenterY=0 CenterZ=0 NormalX=0 NormalY=0 NormalZ=1 AngleXU=0 Radius=2.75 StartAngle=1.5708 EndAngle=2.35619
    g17: GeomPoint [constr] X=0 Y=10 Z=0
    g18: GeomPoint [constr] X=-10 Y=10 Z=0
    g19: LineSegment StartX=-9.70711 StartY=9.70711 StartZ=0 EndX=-1.94454 EndY=1.94454 EndZ=0
    g20: LineSegment StartX=2e-16 StartY=2.75 StartZ=0 EndX=0 EndY=4 EndZ=0
    g21: LineSegment [constr] StartX=-4.46967 StartY=5.53033 StartZ=0 EndX=-5 EndY=5 EndZ=0
  constraints (55):
    c: Radius(g0) = 1
    c: Horizontal(g3)
    c: Parallel(g2,g4)
    c: Vertical(g6)
    c: Tangent(g2,g7) = 1.5708
    c: Tangent(g3,g7) = 1.5708
    c: Tangent(g1,g8) = 1.5708
    c: Tangent(g2,g8) = 1.5708
    c: Radius(g7) = 0.25
    c: Tangent(g1,g0) = 1.5708
    c: PointOnObject(g9,g7)
    c: Horizontal(g9,g7)
    c: PointOnObject(g11,g4)
    c: PointOnObject(g11,g5)
    c: Tangent(g4,g10) = -1.5708
    c: Tangent(g5,g10) = -1.5708
    c: PointOnObject(g13,g4)
    c: PointOnObject(g13,g6)
    c: Tangent(g4,g12) = -1.5708
    c: Tangent(g6,g12) = -1.5708
    c: PointOnObject(g15,g3)
    c: PointOnObject(g15,g6)
    c: Tangent(g3,g14) = -1.5708
    c: Tangent(g6,g14) = -1.5708
    c: Equal(g10,g12)
    c: PointOnObject(g5,g-2)
    c: Coincident(g16,g-1)
    c: PointOnObject(g16,g-2)
    c: PointOnObject(g17,g-2)
    c: PointOnObject(g17,g1)
    c: PointOnObject(g18,g1)
    c: Coincident(g19,g0)
    c: Coincident(g16,g19)
    c: PointOnObject(g0,g19)
    c: PointOnObject(g18,g19)
    c: Parallel(g19,g4)
    c: DistanceX(g18) = -10
    c: DistanceY(g18) = 10
    c: PointOnObject(g16,g19)
    c: Horizontal(g5)
    c: Coincident(g20,g16)
    c: Coincident(g20,g5)
    c: Horizontal(g1)
    c: DistanceX(g15) = -6
    c: DistanceX(g9) = -3.05
    c: DistanceY(g3,g1) = 2
    c: Radius(g10) = 0.5
    c: Radius(g16) = 2.75
    c: DistanceY(g5) = 4
    c: PointOnObject(g21,g4)
    c: Perpendicular(g19,g21)
    c: Distance(g21) = 0.75
    c: Symmetric(g16,g18,g21)
    c: Equal(g14,g7)
    c: Equal(g8,g12)
FEATURE [PartDesign::Pad] Pad
  Direction = (0,0,1)
  Length = 300
  Length2 = 10
  Midplane = true
  Profile = -> Sketch
  ReferenceAxis = -> Sketch [N_Axis]
  Suppressed = false
  Type = 0
  expr: Length = Spreadsheet.side_length - 40
FEATURE [PartDesign::Mirrored] Mirrored
  MirrorPlane = -> Pad [Face4]
  Suppressed = false
  TransformMode = 0
FEATURE [PartDesign::Mirrored] Mirrored001
  MirrorPlane = -> Sketch [V_Axis]
  Suppressed = false
  TransformMode = 0
FEATURE [PartDesign::Mirrored] Mirrored002
  MirrorPlane = -> XZ_Plane005
  Suppressed = false
  TransformMode = 0
FEATURE [PartDesign::MultiTransform] MultiTransform
  BaseFeature = -> Pad
  Originals = -> [Pad]
  Refine = true
  Suppressed = false
  TransformMode = 0
  Transformations = -> [Mirrored,Mirrored001,Mirrored002]
FEATURE [PartDesign::Body] Body  label="horizontal-extrusion"
  AllowCompound = false
  Group = -> [Sketch,Pad,MultiTransform,Mirrored,Mirrored001,Mirrored002]
  Origin = -> Origin005
  Placement = pos=(0,160,210) rot=(0,1,0;1.5708rad)
  Tip = -> MultiTransform
  expr: .Placement.Base.y = Spreadsheet.side_length / 2 - 10
  expr: .Placement.Base.z = Spreadsheet.height / 2 - 10
COMPONENT P23 — same part as P14; its construction recipe is shown at P14.
